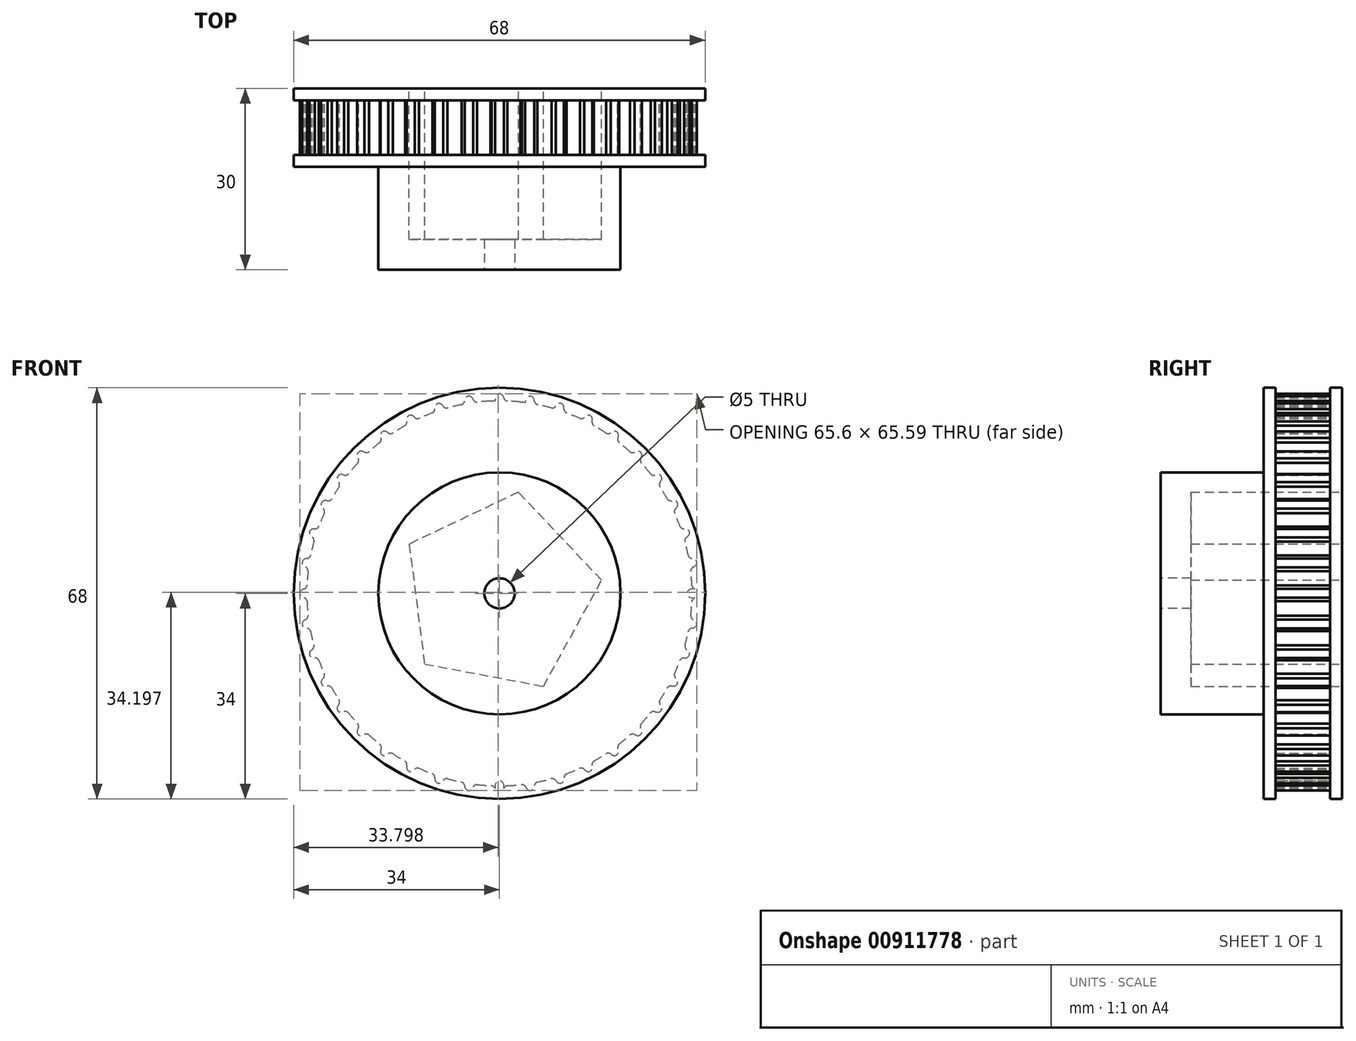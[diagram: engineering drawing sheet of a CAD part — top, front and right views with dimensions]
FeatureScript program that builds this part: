
annotation { "Feature Type Name" : "Feature", "Feature Type Description" : "" }
export const myFeature = defineFeature(function(context is Context, id is Id, definition is map)
    precondition{}
    {
        {
            var Q0;
            Q0=qCreatedBy(makeId("Front.planeOp"),FACE);
            var sketch = newSketch(context, id + "F0", { "sketchPlane" : qUnion([Q0])});
            skCircle(sketch, "E0", {"center": v(0, 0) * mm, "radius": 31.83 * mm});
            skEllipse(sketch, "E1", {"center": v(0, 32) * mm, "majorRadius": 1 * mm, "minorRadius": 0.76 * mm, "majorAxis": v(0, 1)});
            skArc(sketch, "E2", {"start": v(-1.5, 31.8) * mm, "mid": v(-1.02, 31.91) * mm, "end": v(-0.72, 32.3) * mm});
            skArc(sketch, "E3", {"start": v(0.73, 32.28) * mm, "mid": v(1.02, 31.92) * mm, "end": v(1.47, 31.8) * mm});
            skArc(sketch, "E4.1.0", {"start": v(-6.45, 31.17) * mm, "mid": v(-6, 31.36) * mm, "end": v(-5.76, 31.8) * mm});
            skEllipse(sketch, "E4.1.1", {"center": v(-5, 31.6) * mm, "majorRadius": 1 * mm, "minorRadius": 0.76 * mm, "majorAxis": v(-0.16, 0.99)});
            skArc(sketch, "E4.1.2", {"start": v(-4.33, 32) * mm, "mid": v(-3.99, 31.68) * mm, "end": v(-3.52, 31.63) * mm});
            skArc(sketch, "E4.2.0", {"start": v(-11.25, 29.78) * mm, "mid": v(-10.83, 30.04) * mm, "end": v(-10.67, 30.5) * mm});
            skEllipse(sketch, "E4.2.1", {"center": v(-9.89, 30.44) * mm, "majorRadius": 1 * mm, "minorRadius": 0.76 * mm, "majorAxis": v(-0.3, 0.95)});
            skArc(sketch, "E4.2.2", {"start": v(-9.28, 30.93) * mm, "mid": v(-8.9, 30.67) * mm, "end": v(-8.43, 30.7) * mm});
            skArc(sketch, "E4.3.0", {"start": v(-15.77, 27.65) * mm, "mid": v(-15.4, 27.97) * mm, "end": v(-15.3, 28.46) * mm});
            skEllipse(sketch, "E4.3.1", {"center": v(-14.53, 28.52) * mm, "majorRadius": 1 * mm, "minorRadius": 0.76 * mm, "majorAxis": v(-0.45, 0.9)});
            skArc(sketch, "E4.3.2", {"start": v(-14, 29.1) * mm, "mid": v(-13.58, 28.9) * mm, "end": v(-13.12, 29) * mm});
            skArc(sketch, "E4.4.0", {"start": v(-19.9, 24.84) * mm, "mid": v(-19.58, 25.22) * mm, "end": v(-19.57, 25.71) * mm});
            skEllipse(sketch, "E4.4.1", {"center": v(-18.8, 25.9) * mm, "majorRadius": 1 * mm, "minorRadius": 0.76 * mm, "majorAxis": v(-0.59, 0.8)});
            skArc(sketch, "E4.4.2", {"start": v(-18.39, 26.54) * mm, "mid": v(-17.93, 26.42) * mm, "end": v(-17.5, 26.59) * mm});
            skArc(sketch, "E4.5.0", {"start": v(-23.54, 21.42) * mm, "mid": v(-23.29, 21.85) * mm, "end": v(-23.35, 22.33) * mm});
            skEllipse(sketch, "E4.5.1", {"center": v(-22.63, 22.63) * mm, "majorRadius": 1 * mm, "minorRadius": 0.76 * mm, "majorAxis": v(-0.7, 0.7)});
            skArc(sketch, "E4.5.2", {"start": v(-22.31, 23.34) * mm, "mid": v(-21.85, 23.29) * mm, "end": v(-21.44, 23.52) * mm});
            skArc(sketch, "E4.6.0", {"start": v(-26.6, 17.48) * mm, "mid": v(-26.42, 17.93) * mm, "end": v(-26.56, 18.4) * mm});
            skEllipse(sketch, "E4.6.1", {"center": v(-25.9, 18.81) * mm, "majorRadius": 1 * mm, "minorRadius": 0.76 * mm, "majorAxis": v(-0.8, 0.59)});
            skArc(sketch, "E4.6.2", {"start": v(-25.69, 19.56) * mm, "mid": v(-25.22, 19.58) * mm, "end": v(-24.86, 19.88) * mm});
            skArc(sketch, "E4.7.0", {"start": v(-29, 13.1) * mm, "mid": v(-28.9, 13.58) * mm, "end": v(-29.1, 14.03) * mm});
            skEllipse(sketch, "E4.7.1", {"center": v(-28.51, 14.53) * mm, "majorRadius": 1 * mm, "minorRadius": 0.76 * mm, "majorAxis": v(-0.9, 0.45)});
            skArc(sketch, "E4.7.2", {"start": v(-28.43, 15.3) * mm, "mid": v(-27.97, 15.4) * mm, "end": v(-27.66, 15.75) * mm});
            skArc(sketch, "E4.8.0", {"start": v(-30.7, 8.4) * mm, "mid": v(-30.67, 8.9) * mm, "end": v(-30.94, 9.3) * mm});
            skEllipse(sketch, "E4.8.1", {"center": v(-30.44, 9.9) * mm, "majorRadius": 1 * mm, "minorRadius": 0.76 * mm, "majorAxis": v(-0.95, 0.3)});
            skArc(sketch, "E4.8.2", {"start": v(-30.48, 10.67) * mm, "mid": v(-30.04, 10.83) * mm, "end": v(-29.78, 11.22) * mm});
            skArc(sketch, "E4.9.0", {"start": v(-31.64, 3.5) * mm, "mid": v(-31.68, 3.99) * mm, "end": v(-32.02, 4.34) * mm});
            skEllipse(sketch, "E4.9.1", {"center": v(-31.6, 5) * mm, "majorRadius": 1 * mm, "minorRadius": 0.76 * mm, "majorAxis": v(-0.99, 0.16)});
            skArc(sketch, "E4.9.2", {"start": v(-31.77, 5.77) * mm, "mid": v(-31.36, 6) * mm, "end": v(-31.17, 6.43) * mm});
            skArc(sketch, "E4.10.0", {"start": v(-31.8, -1.5) * mm, "mid": v(-31.91, -1.02) * mm, "end": v(-32.3, -0.72) * mm});
            skEllipse(sketch, "E4.10.1", {"center": v(-32, 0) * mm, "majorRadius": 1 * mm, "minorRadius": 0.76 * mm, "majorAxis": v(-1, 0)});
            skArc(sketch, "E4.10.2", {"start": v(-32.28, 0.73) * mm, "mid": v(-31.92, 1.02) * mm, "end": v(-31.8, 1.47) * mm});
            skArc(sketch, "E4.11.0", {"start": v(-31.17, -6.45) * mm, "mid": v(-31.36, -6) * mm, "end": v(-31.8, -5.76) * mm});
            skEllipse(sketch, "E4.11.1", {"center": v(-31.6, -5) * mm, "majorRadius": 1 * mm, "minorRadius": 0.76 * mm, "majorAxis": v(-0.99, -0.16)});
            skArc(sketch, "E4.11.2", {"start": v(-32, -4.33) * mm, "mid": v(-31.68, -3.99) * mm, "end": v(-31.63, -3.52) * mm});
            skArc(sketch, "E4.12.0", {"start": v(-29.78, -11.25) * mm, "mid": v(-30.04, -10.83) * mm, "end": v(-30.5, -10.67) * mm});
            skEllipse(sketch, "E4.12.1", {"center": v(-30.44, -9.89) * mm, "majorRadius": 1 * mm, "minorRadius": 0.76 * mm, "majorAxis": v(-0.95, -0.3)});
            skArc(sketch, "E4.12.2", {"start": v(-30.93, -9.28) * mm, "mid": v(-30.67, -8.9) * mm, "end": v(-30.7, -8.43) * mm});
            skArc(sketch, "E4.13.0", {"start": v(-27.65, -15.77) * mm, "mid": v(-27.97, -15.4) * mm, "end": v(-28.46, -15.3) * mm});
            skEllipse(sketch, "E4.13.1", {"center": v(-28.52, -14.53) * mm, "majorRadius": 1 * mm, "minorRadius": 0.76 * mm, "majorAxis": v(-0.9, -0.45)});
            skArc(sketch, "E4.13.2", {"start": v(-29.1, -14) * mm, "mid": v(-28.9, -13.58) * mm, "end": v(-29, -13.12) * mm});
            skArc(sketch, "E4.14.0", {"start": v(-24.84, -19.9) * mm, "mid": v(-25.22, -19.58) * mm, "end": v(-25.71, -19.57) * mm});
            skEllipse(sketch, "E4.14.1", {"center": v(-25.9, -18.8) * mm, "majorRadius": 1 * mm, "minorRadius": 0.76 * mm, "majorAxis": v(-0.8, -0.59)});
            skArc(sketch, "E4.14.2", {"start": v(-26.54, -18.39) * mm, "mid": v(-26.42, -17.93) * mm, "end": v(-26.59, -17.5) * mm});
            skArc(sketch, "E4.15.0", {"start": v(-21.42, -23.54) * mm, "mid": v(-21.85, -23.29) * mm, "end": v(-22.33, -23.35) * mm});
            skEllipse(sketch, "E4.15.1", {"center": v(-22.63, -22.63) * mm, "majorRadius": 1 * mm, "minorRadius": 0.76 * mm, "majorAxis": v(-0.7, -0.7)});
            skArc(sketch, "E4.15.2", {"start": v(-23.34, -22.31) * mm, "mid": v(-23.29, -21.85) * mm, "end": v(-23.52, -21.44) * mm});
            skArc(sketch, "E4.16.0", {"start": v(-17.48, -26.6) * mm, "mid": v(-17.93, -26.42) * mm, "end": v(-18.4, -26.56) * mm});
            skEllipse(sketch, "E4.16.1", {"center": v(-18.81, -25.9) * mm, "majorRadius": 1 * mm, "minorRadius": 0.76 * mm, "majorAxis": v(-0.59, -0.8)});
            skArc(sketch, "E4.16.2", {"start": v(-19.56, -25.69) * mm, "mid": v(-19.58, -25.22) * mm, "end": v(-19.88, -24.86) * mm});
            skArc(sketch, "E4.17.0", {"start": v(-13.1, -29) * mm, "mid": v(-13.58, -28.9) * mm, "end": v(-14.03, -29.1) * mm});
            skEllipse(sketch, "E4.17.1", {"center": v(-14.53, -28.51) * mm, "majorRadius": 1 * mm, "minorRadius": 0.76 * mm, "majorAxis": v(-0.45, -0.9)});
            skArc(sketch, "E4.17.2", {"start": v(-15.3, -28.43) * mm, "mid": v(-15.4, -27.97) * mm, "end": v(-15.75, -27.66) * mm});
            skArc(sketch, "E4.18.0", {"start": v(-8.4, -30.7) * mm, "mid": v(-8.9, -30.67) * mm, "end": v(-9.3, -30.94) * mm});
            skEllipse(sketch, "E4.18.1", {"center": v(-9.9, -30.44) * mm, "majorRadius": 1 * mm, "minorRadius": 0.76 * mm, "majorAxis": v(-0.3, -0.95)});
            skArc(sketch, "E4.18.2", {"start": v(-10.67, -30.48) * mm, "mid": v(-10.83, -30.04) * mm, "end": v(-11.22, -29.78) * mm});
            skArc(sketch, "E4.19.0", {"start": v(-3.5, -31.64) * mm, "mid": v(-3.99, -31.68) * mm, "end": v(-4.34, -32.02) * mm});
            skEllipse(sketch, "E4.19.1", {"center": v(-5, -31.6) * mm, "majorRadius": 1 * mm, "minorRadius": 0.76 * mm, "majorAxis": v(-0.16, -0.99)});
            skArc(sketch, "E4.19.2", {"start": v(-5.77, -31.77) * mm, "mid": v(-6, -31.36) * mm, "end": v(-6.43, -31.17) * mm});
            skArc(sketch, "E4.20.0", {"start": v(1.5, -31.8) * mm, "mid": v(1.02, -31.91) * mm, "end": v(0.72, -32.3) * mm});
            skEllipse(sketch, "E4.20.1", {"center": v(0, -32) * mm, "majorRadius": 1 * mm, "minorRadius": 0.76 * mm, "majorAxis": v(0, -1)});
            skArc(sketch, "E4.20.2", {"start": v(-0.73, -32.28) * mm, "mid": v(-1.02, -31.92) * mm, "end": v(-1.47, -31.8) * mm});
            skArc(sketch, "E4.21.0", {"start": v(6.45, -31.17) * mm, "mid": v(6, -31.36) * mm, "end": v(5.76, -31.8) * mm});
            skEllipse(sketch, "E4.21.1", {"center": v(5, -31.6) * mm, "majorRadius": 1 * mm, "minorRadius": 0.76 * mm, "majorAxis": v(0.16, -0.99)});
            skArc(sketch, "E4.21.2", {"start": v(4.33, -32) * mm, "mid": v(3.99, -31.68) * mm, "end": v(3.52, -31.63) * mm});
            skArc(sketch, "E4.22.0", {"start": v(11.25, -29.78) * mm, "mid": v(10.83, -30.04) * mm, "end": v(10.67, -30.5) * mm});
            skEllipse(sketch, "E4.22.1", {"center": v(9.89, -30.44) * mm, "majorRadius": 1 * mm, "minorRadius": 0.76 * mm, "majorAxis": v(0.3, -0.95)});
            skArc(sketch, "E4.22.2", {"start": v(9.28, -30.93) * mm, "mid": v(8.9, -30.67) * mm, "end": v(8.43, -30.7) * mm});
            skArc(sketch, "E4.23.0", {"start": v(15.77, -27.65) * mm, "mid": v(15.4, -27.97) * mm, "end": v(15.3, -28.46) * mm});
            skEllipse(sketch, "E4.23.1", {"center": v(14.53, -28.52) * mm, "majorRadius": 1 * mm, "minorRadius": 0.76 * mm, "majorAxis": v(0.45, -0.9)});
            skArc(sketch, "E4.23.2", {"start": v(14, -29.1) * mm, "mid": v(13.58, -28.9) * mm, "end": v(13.12, -29) * mm});
            skArc(sketch, "E4.24.0", {"start": v(19.9, -24.84) * mm, "mid": v(19.58, -25.22) * mm, "end": v(19.57, -25.71) * mm});
            skEllipse(sketch, "E4.24.1", {"center": v(18.8, -25.9) * mm, "majorRadius": 1 * mm, "minorRadius": 0.76 * mm, "majorAxis": v(0.59, -0.8)});
            skArc(sketch, "E4.24.2", {"start": v(18.39, -26.54) * mm, "mid": v(17.93, -26.42) * mm, "end": v(17.5, -26.59) * mm});
            skArc(sketch, "E4.25.0", {"start": v(23.54, -21.42) * mm, "mid": v(23.29, -21.85) * mm, "end": v(23.35, -22.33) * mm});
            skEllipse(sketch, "E4.25.1", {"center": v(22.63, -22.63) * mm, "majorRadius": 1 * mm, "minorRadius": 0.76 * mm, "majorAxis": v(0.7, -0.7)});
            skArc(sketch, "E4.25.2", {"start": v(22.31, -23.34) * mm, "mid": v(21.85, -23.29) * mm, "end": v(21.44, -23.52) * mm});
            skArc(sketch, "E4.26.0", {"start": v(26.6, -17.48) * mm, "mid": v(26.42, -17.93) * mm, "end": v(26.56, -18.4) * mm});
            skEllipse(sketch, "E4.26.1", {"center": v(25.9, -18.81) * mm, "majorRadius": 1 * mm, "minorRadius": 0.76 * mm, "majorAxis": v(0.8, -0.59)});
            skArc(sketch, "E4.26.2", {"start": v(25.69, -19.56) * mm, "mid": v(25.22, -19.58) * mm, "end": v(24.86, -19.88) * mm});
            skArc(sketch, "E4.27.0", {"start": v(29, -13.1) * mm, "mid": v(28.9, -13.58) * mm, "end": v(29.1, -14.03) * mm});
            skEllipse(sketch, "E4.27.1", {"center": v(28.51, -14.53) * mm, "majorRadius": 1 * mm, "minorRadius": 0.76 * mm, "majorAxis": v(0.9, -0.45)});
            skArc(sketch, "E4.27.2", {"start": v(28.43, -15.3) * mm, "mid": v(27.97, -15.4) * mm, "end": v(27.66, -15.75) * mm});
            skArc(sketch, "E4.28.0", {"start": v(30.7, -8.4) * mm, "mid": v(30.67, -8.9) * mm, "end": v(30.94, -9.3) * mm});
            skEllipse(sketch, "E4.28.1", {"center": v(30.44, -9.9) * mm, "majorRadius": 1 * mm, "minorRadius": 0.76 * mm, "majorAxis": v(0.95, -0.3)});
            skArc(sketch, "E4.28.2", {"start": v(30.48, -10.67) * mm, "mid": v(30.04, -10.83) * mm, "end": v(29.78, -11.22) * mm});
            skArc(sketch, "E4.29.0", {"start": v(31.64, -3.5) * mm, "mid": v(31.68, -3.99) * mm, "end": v(32.02, -4.34) * mm});
            skEllipse(sketch, "E4.29.1", {"center": v(31.6, -5) * mm, "majorRadius": 1 * mm, "minorRadius": 0.76 * mm, "majorAxis": v(0.99, -0.16)});
            skArc(sketch, "E4.29.2", {"start": v(31.77, -5.77) * mm, "mid": v(31.36, -6) * mm, "end": v(31.17, -6.43) * mm});
            skArc(sketch, "E4.30.0", {"start": v(31.8, 1.5) * mm, "mid": v(31.91, 1.02) * mm, "end": v(32.3, 0.72) * mm});
            skEllipse(sketch, "E4.30.1", {"center": v(32, 0) * mm, "majorRadius": 1 * mm, "minorRadius": 0.76 * mm, "majorAxis": v(1, 0)});
            skArc(sketch, "E4.30.2", {"start": v(32.28, -0.73) * mm, "mid": v(31.92, -1.02) * mm, "end": v(31.8, -1.47) * mm});
            skArc(sketch, "E4.31.0", {"start": v(31.17, 6.45) * mm, "mid": v(31.36, 6) * mm, "end": v(31.8, 5.76) * mm});
            skEllipse(sketch, "E4.31.1", {"center": v(31.6, 5) * mm, "majorRadius": 1 * mm, "minorRadius": 0.76 * mm, "majorAxis": v(0.99, 0.16)});
            skArc(sketch, "E4.31.2", {"start": v(32, 4.33) * mm, "mid": v(31.68, 3.99) * mm, "end": v(31.63, 3.52) * mm});
            skArc(sketch, "E4.32.0", {"start": v(29.78, 11.25) * mm, "mid": v(30.04, 10.83) * mm, "end": v(30.5, 10.67) * mm});
            skEllipse(sketch, "E4.32.1", {"center": v(30.44, 9.89) * mm, "majorRadius": 1 * mm, "minorRadius": 0.76 * mm, "majorAxis": v(0.95, 0.3)});
            skArc(sketch, "E4.32.2", {"start": v(30.93, 9.28) * mm, "mid": v(30.67, 8.9) * mm, "end": v(30.7, 8.43) * mm});
            skArc(sketch, "E4.33.0", {"start": v(27.65, 15.77) * mm, "mid": v(27.97, 15.4) * mm, "end": v(28.46, 15.3) * mm});
            skEllipse(sketch, "E4.33.1", {"center": v(28.52, 14.53) * mm, "majorRadius": 1 * mm, "minorRadius": 0.76 * mm, "majorAxis": v(0.9, 0.45)});
            skArc(sketch, "E4.33.2", {"start": v(29.1, 14) * mm, "mid": v(28.9, 13.58) * mm, "end": v(29, 13.12) * mm});
            skArc(sketch, "E4.34.0", {"start": v(24.84, 19.9) * mm, "mid": v(25.22, 19.58) * mm, "end": v(25.71, 19.57) * mm});
            skEllipse(sketch, "E4.34.1", {"center": v(25.9, 18.8) * mm, "majorRadius": 1 * mm, "minorRadius": 0.76 * mm, "majorAxis": v(0.8, 0.59)});
            skArc(sketch, "E4.34.2", {"start": v(26.54, 18.39) * mm, "mid": v(26.42, 17.93) * mm, "end": v(26.59, 17.5) * mm});
            skArc(sketch, "E4.35.0", {"start": v(21.42, 23.54) * mm, "mid": v(21.85, 23.29) * mm, "end": v(22.33, 23.35) * mm});
            skEllipse(sketch, "E4.35.1", {"center": v(22.63, 22.63) * mm, "majorRadius": 1 * mm, "minorRadius": 0.76 * mm, "majorAxis": v(0.7, 0.7)});
            skArc(sketch, "E4.35.2", {"start": v(23.34, 22.31) * mm, "mid": v(23.29, 21.85) * mm, "end": v(23.52, 21.44) * mm});
            skArc(sketch, "E4.36.0", {"start": v(17.48, 26.6) * mm, "mid": v(17.93, 26.42) * mm, "end": v(18.4, 26.56) * mm});
            skEllipse(sketch, "E4.36.1", {"center": v(18.81, 25.9) * mm, "majorRadius": 1 * mm, "minorRadius": 0.76 * mm, "majorAxis": v(0.59, 0.8)});
            skArc(sketch, "E4.36.2", {"start": v(19.56, 25.69) * mm, "mid": v(19.58, 25.22) * mm, "end": v(19.88, 24.86) * mm});
            skArc(sketch, "E4.37.0", {"start": v(13.1, 29) * mm, "mid": v(13.58, 28.9) * mm, "end": v(14.03, 29.1) * mm});
            skEllipse(sketch, "E4.37.1", {"center": v(14.53, 28.51) * mm, "majorRadius": 1 * mm, "minorRadius": 0.76 * mm, "majorAxis": v(0.45, 0.9)});
            skArc(sketch, "E4.37.2", {"start": v(15.3, 28.43) * mm, "mid": v(15.4, 27.97) * mm, "end": v(15.75, 27.66) * mm});
            skArc(sketch, "E4.38.0", {"start": v(8.4, 30.7) * mm, "mid": v(8.9, 30.67) * mm, "end": v(9.3, 30.94) * mm});
            skEllipse(sketch, "E4.38.1", {"center": v(9.9, 30.44) * mm, "majorRadius": 1 * mm, "minorRadius": 0.76 * mm, "majorAxis": v(0.3, 0.95)});
            skArc(sketch, "E4.38.2", {"start": v(10.67, 30.48) * mm, "mid": v(10.83, 30.04) * mm, "end": v(11.22, 29.78) * mm});
            skArc(sketch, "E4.39.0", {"start": v(3.5, 31.64) * mm, "mid": v(3.99, 31.68) * mm, "end": v(4.34, 32.02) * mm});
            skEllipse(sketch, "E4.39.1", {"center": v(5, 31.6) * mm, "majorRadius": 1 * mm, "minorRadius": 0.76 * mm, "majorAxis": v(0.16, 0.99)});
            skArc(sketch, "E4.39.2", {"start": v(5.77, 31.77) * mm, "mid": v(6, 31.36) * mm, "end": v(6.43, 31.17) * mm});
            skSolve(sketch);
        }
        {
            var Q0;
            {var subQ0=sQuery(id+"F0.wireOp",EDGE,"E4.9.1");var subQ1=sQuery(id+"F0.wireOp",EDGE,"E0");var subQ2=makeQuery(id+"F0.imprint","INTERSECT",VERTEX,{"disambiguationData":[OD(0.0)],"derivedFrom":[subQ1,subQ0]});Q0=makeQuery(id+"F0.imprint","IMPRINT",FACE,{"disambiguationData":[TD([[makeQuery(id+"F0.imprint","IMPRINT",EDGE,{"disambiguationData":[TD([[subQ2,-1.0]])],"derivedFrom":subQ1}),-1.0]])]});}
            var Q1;
            {var subQ1=sQuery(id+"F0.wireOp",EDGE,"E0");var subQ208=sQuery(id+"F0.wireOp",EDGE,"E4.30.0");var subQ210=makeQuery(id+"F0.imprint","INTERSECT",VERTEX,{"disambiguationData":[OD(1.0)],"derivedFrom":[subQ1,subQ208]});Q1=makeQuery(id+"F0.imprint","IMPRINT",FACE,{"disambiguationData":[TD([[makeQuery(id+"F0.imprint","IMPRINT",EDGE,{"disambiguationData":[TD([[subQ210,1.0]])],"derivedFrom":subQ1}),1.0]])]});}
            var Q2;
            {var subQ0=sQuery(id+"F0.wireOp",EDGE,"E4.4.1");var subQ1=sQuery(id+"F0.wireOp",EDGE,"E0");var subQ2=makeQuery(id+"F0.imprint","INTERSECT",VERTEX,{"disambiguationData":[OD(0.0)],"derivedFrom":[subQ1,subQ0]});Q2=makeQuery(id+"F0.imprint","IMPRINT",FACE,{"disambiguationData":[TD([[makeQuery(id+"F0.imprint","IMPRINT",EDGE,{"disambiguationData":[TD([[subQ2,-1.0]])],"derivedFrom":subQ1}),1.0]])]});}
            var Q3;
            {var subQ0=sQuery(id+"F0.wireOp",EDGE,"E4.8.0");var subQ1=sQuery(id+"F0.wireOp",EDGE,"E0");var subQ2=makeQuery(id+"F0.imprint","INTERSECT",VERTEX,{"disambiguationData":[OD(1.0)],"derivedFrom":[subQ1,subQ0]});Q3=makeQuery(id+"F0.imprint","IMPRINT",FACE,{"disambiguationData":[TD([[makeQuery(id+"F0.imprint","IMPRINT",EDGE,{"disambiguationData":[TD([[subQ2,1.0]])],"derivedFrom":subQ1}),-1.0]])]});}
            var Q4;
            {var subQ0=sQuery(id+"F0.wireOp",EDGE,"E4.32.1");var subQ1=sQuery(id+"F0.wireOp",EDGE,"E0");var subQ2=makeQuery(id+"F0.imprint","INTERSECT",VERTEX,{"disambiguationData":[OD(0.0)],"derivedFrom":[subQ1,subQ0]});Q4=makeQuery(id+"F0.imprint","IMPRINT",FACE,{"disambiguationData":[TD([[makeQuery(id+"F0.imprint","IMPRINT",EDGE,{"disambiguationData":[TD([[subQ2,-1.0]])],"derivedFrom":subQ1}),-1.0]])]});}
            var Q5;
            {var subQ0=sQuery(id+"F0.wireOp",EDGE,"E4.30.1");var subQ1=sQuery(id+"F0.wireOp",EDGE,"E0");var subQ2=makeQuery(id+"F0.imprint","INTERSECT",VERTEX,{"disambiguationData":[OD(0.0)],"derivedFrom":[subQ1,subQ0]});Q5=makeQuery(id+"F0.imprint","IMPRINT",FACE,{"disambiguationData":[TD([[makeQuery(id+"F0.imprint","IMPRINT",EDGE,{"disambiguationData":[TD([[subQ2,1.0]])],"derivedFrom":subQ1}),1.0]])]});}
            var Q6;
            {var subQ0=sQuery(id+"F0.wireOp",EDGE,"E4.36.1");var subQ1=sQuery(id+"F0.wireOp",EDGE,"E0");var subQ2=makeQuery(id+"F0.imprint","INTERSECT",VERTEX,{"disambiguationData":[OD(0.0)],"derivedFrom":[subQ1,subQ0]});Q6=makeQuery(id+"F0.imprint","IMPRINT",FACE,{"disambiguationData":[TD([[makeQuery(id+"F0.imprint","IMPRINT",EDGE,{"disambiguationData":[TD([[subQ2,-1.0]])],"derivedFrom":subQ1}),1.0]])]});}
            var Q7;
            {var subQ0=sQuery(id+"F0.wireOp",EDGE,"E4.10.1");var subQ1=sQuery(id+"F0.wireOp",EDGE,"E0");var subQ2=makeQuery(id+"F0.imprint","INTERSECT",VERTEX,{"disambiguationData":[OD(0.0)],"derivedFrom":[subQ1,subQ0]});Q7=makeQuery(id+"F0.imprint","IMPRINT",FACE,{"disambiguationData":[TD([[makeQuery(id+"F0.imprint","IMPRINT",EDGE,{"disambiguationData":[TD([[subQ2,-1.0]])],"derivedFrom":subQ1}),1.0]])]});}
            var Q8;
            {var subQ0=sQuery(id+"F0.wireOp",EDGE,"E4.6.1");var subQ1=sQuery(id+"F0.wireOp",EDGE,"E0");var subQ2=makeQuery(id+"F0.imprint","INTERSECT",VERTEX,{"disambiguationData":[OD(0.0)],"derivedFrom":[subQ1,subQ0]});Q8=makeQuery(id+"F0.imprint","IMPRINT",FACE,{"disambiguationData":[TD([[makeQuery(id+"F0.imprint","IMPRINT",EDGE,{"disambiguationData":[TD([[subQ2,-1.0]])],"derivedFrom":subQ1}),1.0]])]});}
            var Q9;
            {var subQ0=sQuery(id+"F0.wireOp",EDGE,"E4.26.1");var subQ1=sQuery(id+"F0.wireOp",EDGE,"E0");var subQ2=makeQuery(id+"F0.imprint","INTERSECT",VERTEX,{"disambiguationData":[OD(0.0)],"derivedFrom":[subQ1,subQ0]});Q9=makeQuery(id+"F0.imprint","IMPRINT",FACE,{"disambiguationData":[TD([[makeQuery(id+"F0.imprint","IMPRINT",EDGE,{"disambiguationData":[TD([[subQ2,-1.0]])],"derivedFrom":subQ1}),1.0]])]});}
            var Q10;
            {var subQ0=sQuery(id+"F0.wireOp",EDGE,"E4.21.1");var subQ1=sQuery(id+"F0.wireOp",EDGE,"E0");var subQ2=makeQuery(id+"F0.imprint","INTERSECT",VERTEX,{"disambiguationData":[OD(0.0)],"derivedFrom":[subQ1,subQ0]});Q10=makeQuery(id+"F0.imprint","IMPRINT",FACE,{"disambiguationData":[TD([[makeQuery(id+"F0.imprint","IMPRINT",EDGE,{"disambiguationData":[TD([[subQ2,-1.0]])],"derivedFrom":subQ1}),1.0]])]});}
            var Q11;
            {var subQ0=sQuery(id+"F0.wireOp",EDGE,"E4.18.1");var subQ1=sQuery(id+"F0.wireOp",EDGE,"E0");var subQ2=makeQuery(id+"F0.imprint","INTERSECT",VERTEX,{"disambiguationData":[OD(0.0)],"derivedFrom":[subQ1,subQ0]});Q11=makeQuery(id+"F0.imprint","IMPRINT",FACE,{"disambiguationData":[TD([[makeQuery(id+"F0.imprint","IMPRINT",EDGE,{"disambiguationData":[TD([[subQ2,-1.0]])],"derivedFrom":subQ1}),-1.0]])]});}
            var Q12;
            {var subQ0=sQuery(id+"F0.wireOp",EDGE,"E1");var subQ1=sQuery(id+"F0.wireOp",EDGE,"E0");var subQ2=makeQuery(id+"F0.imprint","INTERSECT",VERTEX,{"disambiguationData":[OD(0.0)],"derivedFrom":[subQ1,subQ0]});Q12=makeQuery(id+"F0.imprint","IMPRINT",FACE,{"disambiguationData":[TD([[makeQuery(id+"F0.imprint","IMPRINT",EDGE,{"disambiguationData":[TD([[subQ2,-1.0]])],"derivedFrom":subQ1}),1.0]])]});}
            var Q13;
            {var subQ0=sQuery(id+"F0.wireOp",EDGE,"E4.33.1");var subQ1=sQuery(id+"F0.wireOp",EDGE,"E0");var subQ2=makeQuery(id+"F0.imprint","INTERSECT",VERTEX,{"disambiguationData":[OD(0.0)],"derivedFrom":[subQ1,subQ0]});Q13=makeQuery(id+"F0.imprint","IMPRINT",FACE,{"disambiguationData":[TD([[makeQuery(id+"F0.imprint","IMPRINT",EDGE,{"disambiguationData":[TD([[subQ2,-1.0]])],"derivedFrom":subQ1}),1.0]])]});}
            var Q14;
            {var subQ0=sQuery(id+"F0.wireOp",EDGE,"E4.34.1");var subQ1=sQuery(id+"F0.wireOp",EDGE,"E0");var subQ2=makeQuery(id+"F0.imprint","INTERSECT",VERTEX,{"disambiguationData":[OD(0.0)],"derivedFrom":[subQ1,subQ0]});Q14=makeQuery(id+"F0.imprint","IMPRINT",FACE,{"disambiguationData":[TD([[makeQuery(id+"F0.imprint","IMPRINT",EDGE,{"disambiguationData":[TD([[subQ2,-1.0]])],"derivedFrom":subQ1}),1.0]])]});}
            var Q15;
            {var subQ0=sQuery(id+"F0.wireOp",EDGE,"E4.17.0");var subQ1=sQuery(id+"F0.wireOp",EDGE,"E0");var subQ2=makeQuery(id+"F0.imprint","INTERSECT",VERTEX,{"disambiguationData":[OD(1.0)],"derivedFrom":[subQ1,subQ0]});Q15=makeQuery(id+"F0.imprint","IMPRINT",FACE,{"disambiguationData":[TD([[makeQuery(id+"F0.imprint","IMPRINT",EDGE,{"disambiguationData":[TD([[subQ2,1.0]])],"derivedFrom":subQ1}),-1.0]])]});}
            var Q16;
            {var subQ0=sQuery(id+"F0.wireOp",EDGE,"E4.39.1");var subQ1=sQuery(id+"F0.wireOp",EDGE,"E0");var subQ2=makeQuery(id+"F0.imprint","INTERSECT",VERTEX,{"disambiguationData":[OD(0.0)],"derivedFrom":[subQ1,subQ0]});Q16=makeQuery(id+"F0.imprint","IMPRINT",FACE,{"disambiguationData":[TD([[makeQuery(id+"F0.imprint","IMPRINT",EDGE,{"disambiguationData":[TD([[subQ2,-1.0]])],"derivedFrom":subQ1}),1.0]])]});}
            var Q17;
            {var subQ0=sQuery(id+"F0.wireOp",EDGE,"E4.7.1");var subQ1=sQuery(id+"F0.wireOp",EDGE,"E0");var subQ2=makeQuery(id+"F0.imprint","INTERSECT",VERTEX,{"disambiguationData":[OD(0.0)],"derivedFrom":[subQ1,subQ0]});Q17=makeQuery(id+"F0.imprint","IMPRINT",FACE,{"disambiguationData":[TD([[makeQuery(id+"F0.imprint","IMPRINT",EDGE,{"disambiguationData":[TD([[subQ2,-1.0]])],"derivedFrom":subQ1}),-1.0]])]});}
            var Q18;
            {var subQ0=sQuery(id+"F0.wireOp",EDGE,"E4.33.1");var subQ1=sQuery(id+"F0.wireOp",EDGE,"E0");var subQ2=makeQuery(id+"F0.imprint","INTERSECT",VERTEX,{"disambiguationData":[OD(0.0)],"derivedFrom":[subQ1,subQ0]});Q18=makeQuery(id+"F0.imprint","IMPRINT",FACE,{"disambiguationData":[TD([[makeQuery(id+"F0.imprint","IMPRINT",EDGE,{"disambiguationData":[TD([[subQ2,-1.0]])],"derivedFrom":subQ1}),-1.0]])]});}
            var Q19;
            {var subQ0=sQuery(id+"F0.wireOp",EDGE,"E4.19.1");var subQ1=sQuery(id+"F0.wireOp",EDGE,"E0");var subQ2=makeQuery(id+"F0.imprint","INTERSECT",VERTEX,{"disambiguationData":[OD(0.0)],"derivedFrom":[subQ1,subQ0]});Q19=makeQuery(id+"F0.imprint","IMPRINT",FACE,{"disambiguationData":[TD([[makeQuery(id+"F0.imprint","IMPRINT",EDGE,{"disambiguationData":[TD([[subQ2,-1.0]])],"derivedFrom":subQ1}),-1.0]])]});}
            var Q20;
            {var subQ0=sQuery(id+"F0.wireOp",EDGE,"E4.19.1");var subQ1=sQuery(id+"F0.wireOp",EDGE,"E0");var subQ2=makeQuery(id+"F0.imprint","INTERSECT",VERTEX,{"disambiguationData":[OD(0.0)],"derivedFrom":[subQ1,subQ0]});Q20=makeQuery(id+"F0.imprint","IMPRINT",FACE,{"disambiguationData":[TD([[makeQuery(id+"F0.imprint","IMPRINT",EDGE,{"disambiguationData":[TD([[subQ2,-1.0]])],"derivedFrom":subQ1}),1.0]])]});}
            var Q21;
            {var subQ0=sQuery(id+"F0.wireOp",EDGE,"E4.6.2");var subQ1=sQuery(id+"F0.wireOp",EDGE,"E0");var subQ2=makeQuery(id+"F0.imprint","INTERSECT",VERTEX,{"derivedFrom":[subQ1,subQ0]});Q21=makeQuery(id+"F0.imprint","IMPRINT",FACE,{"disambiguationData":[TD([[makeQuery(id+"F0.imprint","IMPRINT",EDGE,{"disambiguationData":[TD([[subQ2,-1.0]])],"derivedFrom":subQ1}),-1.0]])]});}
            var Q22;
            {var subQ0=sQuery(id+"F0.wireOp",EDGE,"E4.36.1");var subQ1=sQuery(id+"F0.wireOp",EDGE,"E0");var subQ2=makeQuery(id+"F0.imprint","INTERSECT",VERTEX,{"disambiguationData":[OD(0.0)],"derivedFrom":[subQ1,subQ0]});Q22=makeQuery(id+"F0.imprint","IMPRINT",FACE,{"disambiguationData":[TD([[makeQuery(id+"F0.imprint","IMPRINT",EDGE,{"disambiguationData":[TD([[subQ2,-1.0]])],"derivedFrom":subQ1}),-1.0]])]});}
            var Q23;
            {var subQ0=sQuery(id+"F0.wireOp",EDGE,"E4.37.1");var subQ1=sQuery(id+"F0.wireOp",EDGE,"E0");var subQ2=makeQuery(id+"F0.imprint","INTERSECT",VERTEX,{"disambiguationData":[OD(0.0)],"derivedFrom":[subQ1,subQ0]});Q23=makeQuery(id+"F0.imprint","IMPRINT",FACE,{"disambiguationData":[TD([[makeQuery(id+"F0.imprint","IMPRINT",EDGE,{"disambiguationData":[TD([[subQ2,-1.0]])],"derivedFrom":subQ1}),-1.0]])]});}
            var Q24;
            {var subQ0=sQuery(id+"F0.wireOp",EDGE,"E4.27.1");var subQ1=sQuery(id+"F0.wireOp",EDGE,"E0");var subQ2=makeQuery(id+"F0.imprint","INTERSECT",VERTEX,{"disambiguationData":[OD(0.0)],"derivedFrom":[subQ1,subQ0]});Q24=makeQuery(id+"F0.imprint","IMPRINT",FACE,{"disambiguationData":[TD([[makeQuery(id+"F0.imprint","IMPRINT",EDGE,{"disambiguationData":[TD([[subQ2,-1.0]])],"derivedFrom":subQ1}),1.0]])]});}
            var Q25;
            {var subQ0=sQuery(id+"F0.wireOp",EDGE,"E4.26.1");var subQ1=sQuery(id+"F0.wireOp",EDGE,"E0");var subQ2=makeQuery(id+"F0.imprint","INTERSECT",VERTEX,{"disambiguationData":[OD(0.0)],"derivedFrom":[subQ1,subQ0]});Q25=makeQuery(id+"F0.imprint","IMPRINT",FACE,{"disambiguationData":[TD([[makeQuery(id+"F0.imprint","IMPRINT",EDGE,{"disambiguationData":[TD([[subQ2,-1.0]])],"derivedFrom":subQ1}),-1.0]])]});}
            var Q26;
            {var subQ0=sQuery(id+"F0.wireOp",EDGE,"E4.10.1");var subQ1=sQuery(id+"F0.wireOp",EDGE,"E0");var subQ2=makeQuery(id+"F0.imprint","INTERSECT",VERTEX,{"disambiguationData":[OD(0.0)],"derivedFrom":[subQ1,subQ0]});Q26=makeQuery(id+"F0.imprint","IMPRINT",FACE,{"disambiguationData":[TD([[makeQuery(id+"F0.imprint","IMPRINT",EDGE,{"disambiguationData":[TD([[subQ2,-1.0]])],"derivedFrom":subQ1}),-1.0]])]});}
            var Q27;
            {var subQ0=sQuery(id+"F0.wireOp",EDGE,"E4.15.1");var subQ1=sQuery(id+"F0.wireOp",EDGE,"E0");var subQ2=makeQuery(id+"F0.imprint","INTERSECT",VERTEX,{"disambiguationData":[OD(0.0)],"derivedFrom":[subQ1,subQ0]});Q27=makeQuery(id+"F0.imprint","IMPRINT",FACE,{"disambiguationData":[TD([[makeQuery(id+"F0.imprint","IMPRINT",EDGE,{"disambiguationData":[TD([[subQ2,-1.0]])],"derivedFrom":subQ1}),-1.0]])]});}
            var Q28;
            {var subQ0=sQuery(id+"F0.wireOp",EDGE,"E4.20.1");var subQ1=sQuery(id+"F0.wireOp",EDGE,"E0");var subQ2=makeQuery(id+"F0.imprint","INTERSECT",VERTEX,{"disambiguationData":[OD(0.0)],"derivedFrom":[subQ1,subQ0]});Q28=makeQuery(id+"F0.imprint","IMPRINT",FACE,{"disambiguationData":[TD([[makeQuery(id+"F0.imprint","IMPRINT",EDGE,{"disambiguationData":[TD([[subQ2,-1.0]])],"derivedFrom":subQ1}),1.0]])]});}
            var Q29;
            {var subQ0=sQuery(id+"F0.wireOp",EDGE,"E4.31.1");var subQ1=sQuery(id+"F0.wireOp",EDGE,"E0");var subQ2=makeQuery(id+"F0.imprint","INTERSECT",VERTEX,{"disambiguationData":[OD(0.0)],"derivedFrom":[subQ1,subQ0]});Q29=makeQuery(id+"F0.imprint","IMPRINT",FACE,{"disambiguationData":[TD([[makeQuery(id+"F0.imprint","IMPRINT",EDGE,{"disambiguationData":[TD([[subQ2,-1.0]])],"derivedFrom":subQ1}),-1.0]])]});}
            var Q30;
            {var subQ0=sQuery(id+"F0.wireOp",EDGE,"E4.21.1");var subQ1=sQuery(id+"F0.wireOp",EDGE,"E0");var subQ2=makeQuery(id+"F0.imprint","INTERSECT",VERTEX,{"disambiguationData":[OD(0.0)],"derivedFrom":[subQ1,subQ0]});Q30=makeQuery(id+"F0.imprint","IMPRINT",FACE,{"disambiguationData":[TD([[makeQuery(id+"F0.imprint","IMPRINT",EDGE,{"disambiguationData":[TD([[subQ2,-1.0]])],"derivedFrom":subQ1}),-1.0]])]});}
            var Q31;
            {var subQ0=sQuery(id+"F0.wireOp",EDGE,"E4.18.1");var subQ1=sQuery(id+"F0.wireOp",EDGE,"E0");var subQ2=makeQuery(id+"F0.imprint","INTERSECT",VERTEX,{"disambiguationData":[OD(0.0)],"derivedFrom":[subQ1,subQ0]});Q31=makeQuery(id+"F0.imprint","IMPRINT",FACE,{"disambiguationData":[TD([[makeQuery(id+"F0.imprint","IMPRINT",EDGE,{"disambiguationData":[TD([[subQ2,-1.0]])],"derivedFrom":subQ1}),1.0]])]});}
            var Q32;
            {var subQ0=sQuery(id+"F0.wireOp",EDGE,"E4.37.1");var subQ1=sQuery(id+"F0.wireOp",EDGE,"E0");var subQ2=makeQuery(id+"F0.imprint","INTERSECT",VERTEX,{"disambiguationData":[OD(0.0)],"derivedFrom":[subQ1,subQ0]});Q32=makeQuery(id+"F0.imprint","IMPRINT",FACE,{"disambiguationData":[TD([[makeQuery(id+"F0.imprint","IMPRINT",EDGE,{"disambiguationData":[TD([[subQ2,-1.0]])],"derivedFrom":subQ1}),1.0]])]});}
            var Q33;
            {var subQ0=sQuery(id+"F0.wireOp",EDGE,"E4.1.1");var subQ1=sQuery(id+"F0.wireOp",EDGE,"E0");var subQ2=makeQuery(id+"F0.imprint","INTERSECT",VERTEX,{"disambiguationData":[OD(0.0)],"derivedFrom":[subQ1,subQ0]});Q33=makeQuery(id+"F0.imprint","IMPRINT",FACE,{"disambiguationData":[TD([[makeQuery(id+"F0.imprint","IMPRINT",EDGE,{"disambiguationData":[TD([[subQ2,-1.0]])],"derivedFrom":subQ1}),-1.0]])]});}
            var Q34;
            {var subQ0=sQuery(id+"F0.wireOp",EDGE,"E4.12.1");var subQ1=sQuery(id+"F0.wireOp",EDGE,"E0");var subQ2=makeQuery(id+"F0.imprint","INTERSECT",VERTEX,{"disambiguationData":[OD(0.0)],"derivedFrom":[subQ1,subQ0]});Q34=makeQuery(id+"F0.imprint","IMPRINT",FACE,{"disambiguationData":[TD([[makeQuery(id+"F0.imprint","IMPRINT",EDGE,{"disambiguationData":[TD([[subQ2,-1.0]])],"derivedFrom":subQ1}),-1.0]])]});}
            var Q35;
            {var subQ0=sQuery(id+"F0.wireOp",EDGE,"E4.16.1");var subQ1=sQuery(id+"F0.wireOp",EDGE,"E0");var subQ2=makeQuery(id+"F0.imprint","INTERSECT",VERTEX,{"disambiguationData":[OD(0.0)],"derivedFrom":[subQ1,subQ0]});Q35=makeQuery(id+"F0.imprint","IMPRINT",FACE,{"disambiguationData":[TD([[makeQuery(id+"F0.imprint","IMPRINT",EDGE,{"disambiguationData":[TD([[subQ2,-1.0]])],"derivedFrom":subQ1}),1.0]])]});}
            var Q36;
            {var subQ0=sQuery(id+"F0.wireOp",EDGE,"E4.14.1");var subQ1=sQuery(id+"F0.wireOp",EDGE,"E0");var subQ2=makeQuery(id+"F0.imprint","INTERSECT",VERTEX,{"disambiguationData":[OD(0.0)],"derivedFrom":[subQ1,subQ0]});Q36=makeQuery(id+"F0.imprint","IMPRINT",FACE,{"disambiguationData":[TD([[makeQuery(id+"F0.imprint","IMPRINT",EDGE,{"disambiguationData":[TD([[subQ2,-1.0]])],"derivedFrom":subQ1}),1.0]])]});}
            var Q37;
            {var subQ0=sQuery(id+"F0.wireOp",EDGE,"E4.13.1");var subQ1=sQuery(id+"F0.wireOp",EDGE,"E0");var subQ2=makeQuery(id+"F0.imprint","INTERSECT",VERTEX,{"disambiguationData":[OD(0.0)],"derivedFrom":[subQ1,subQ0]});Q37=makeQuery(id+"F0.imprint","IMPRINT",FACE,{"disambiguationData":[TD([[makeQuery(id+"F0.imprint","IMPRINT",EDGE,{"disambiguationData":[TD([[subQ2,-1.0]])],"derivedFrom":subQ1}),-1.0]])]});}
            var Q38;
            {var subQ0=sQuery(id+"F0.wireOp",EDGE,"E4.25.1");var subQ1=sQuery(id+"F0.wireOp",EDGE,"E0");var subQ2=makeQuery(id+"F0.imprint","INTERSECT",VERTEX,{"disambiguationData":[OD(0.0)],"derivedFrom":[subQ1,subQ0]});Q38=makeQuery(id+"F0.imprint","IMPRINT",FACE,{"disambiguationData":[TD([[makeQuery(id+"F0.imprint","IMPRINT",EDGE,{"disambiguationData":[TD([[subQ2,-1.0]])],"derivedFrom":subQ1}),-1.0]])]});}
            var Q39;
            {var subQ0=sQuery(id+"F0.wireOp",EDGE,"E4.32.1");var subQ1=sQuery(id+"F0.wireOp",EDGE,"E0");var subQ2=makeQuery(id+"F0.imprint","INTERSECT",VERTEX,{"disambiguationData":[OD(0.0)],"derivedFrom":[subQ1,subQ0]});Q39=makeQuery(id+"F0.imprint","IMPRINT",FACE,{"disambiguationData":[TD([[makeQuery(id+"F0.imprint","IMPRINT",EDGE,{"disambiguationData":[TD([[subQ2,-1.0]])],"derivedFrom":subQ1}),1.0]])]});}
            var Q40;
            {var subQ0=sQuery(id+"F0.wireOp",EDGE,"E4.24.1");var subQ1=sQuery(id+"F0.wireOp",EDGE,"E0");var subQ2=makeQuery(id+"F0.imprint","INTERSECT",VERTEX,{"disambiguationData":[OD(0.0)],"derivedFrom":[subQ1,subQ0]});Q40=makeQuery(id+"F0.imprint","IMPRINT",FACE,{"disambiguationData":[TD([[makeQuery(id+"F0.imprint","IMPRINT",EDGE,{"disambiguationData":[TD([[subQ2,-1.0]])],"derivedFrom":subQ1}),-1.0]])]});}
            var Q41;
            {var subQ0=sQuery(id+"F0.wireOp",EDGE,"E4.6.1");var subQ1=sQuery(id+"F0.wireOp",EDGE,"E0");var subQ2=makeQuery(id+"F0.imprint","INTERSECT",VERTEX,{"disambiguationData":[OD(0.0)],"derivedFrom":[subQ1,subQ0]});Q41=makeQuery(id+"F0.imprint","IMPRINT",FACE,{"disambiguationData":[TD([[makeQuery(id+"F0.imprint","IMPRINT",EDGE,{"disambiguationData":[TD([[subQ2,-1.0]])],"derivedFrom":subQ1}),-1.0]])]});}
            var Q42;
            {var subQ0=sQuery(id+"F0.wireOp",EDGE,"E4.11.1");var subQ1=sQuery(id+"F0.wireOp",EDGE,"E0");var subQ2=makeQuery(id+"F0.imprint","INTERSECT",VERTEX,{"disambiguationData":[OD(0.0)],"derivedFrom":[subQ1,subQ0]});Q42=makeQuery(id+"F0.imprint","IMPRINT",FACE,{"disambiguationData":[TD([[makeQuery(id+"F0.imprint","IMPRINT",EDGE,{"disambiguationData":[TD([[subQ2,-1.0]])],"derivedFrom":subQ1}),-1.0]])]});}
            var Q43;
            {var subQ0=sQuery(id+"F0.wireOp",EDGE,"E4.2.1");var subQ1=sQuery(id+"F0.wireOp",EDGE,"E0");var subQ2=makeQuery(id+"F0.imprint","INTERSECT",VERTEX,{"disambiguationData":[OD(0.0)],"derivedFrom":[subQ1,subQ0]});Q43=makeQuery(id+"F0.imprint","IMPRINT",FACE,{"disambiguationData":[TD([[makeQuery(id+"F0.imprint","IMPRINT",EDGE,{"disambiguationData":[TD([[subQ2,-1.0]])],"derivedFrom":subQ1}),-1.0]])]});}
            var Q44;
            {var subQ0=sQuery(id+"F0.wireOp",EDGE,"E4.23.1");var subQ1=sQuery(id+"F0.wireOp",EDGE,"E0");var subQ2=makeQuery(id+"F0.imprint","INTERSECT",VERTEX,{"disambiguationData":[OD(0.0)],"derivedFrom":[subQ1,subQ0]});Q44=makeQuery(id+"F0.imprint","IMPRINT",FACE,{"disambiguationData":[TD([[makeQuery(id+"F0.imprint","IMPRINT",EDGE,{"disambiguationData":[TD([[subQ2,-1.0]])],"derivedFrom":subQ1}),-1.0]])]});}
            var Q45;
            {var subQ0=sQuery(id+"F0.wireOp",EDGE,"E4.3.1");var subQ1=sQuery(id+"F0.wireOp",EDGE,"E0");var subQ2=makeQuery(id+"F0.imprint","INTERSECT",VERTEX,{"disambiguationData":[OD(0.0)],"derivedFrom":[subQ1,subQ0]});Q45=makeQuery(id+"F0.imprint","IMPRINT",FACE,{"disambiguationData":[TD([[makeQuery(id+"F0.imprint","IMPRINT",EDGE,{"disambiguationData":[TD([[subQ2,-1.0]])],"derivedFrom":subQ1}),1.0]])]});}
            var Q46;
            {var subQ0=sQuery(id+"F0.wireOp",EDGE,"E4.16.0");var subQ1=sQuery(id+"F0.wireOp",EDGE,"E0");var subQ2=makeQuery(id+"F0.imprint","INTERSECT",VERTEX,{"disambiguationData":[OD(1.0)],"derivedFrom":[subQ1,subQ0]});Q46=makeQuery(id+"F0.imprint","IMPRINT",FACE,{"disambiguationData":[TD([[makeQuery(id+"F0.imprint","IMPRINT",EDGE,{"disambiguationData":[TD([[subQ2,1.0]])],"derivedFrom":subQ1}),-1.0]])]});}
            var Q47;
            {var subQ0=sQuery(id+"F0.wireOp",EDGE,"E4.14.1");var subQ1=sQuery(id+"F0.wireOp",EDGE,"E0");var subQ2=makeQuery(id+"F0.imprint","INTERSECT",VERTEX,{"disambiguationData":[OD(0.0)],"derivedFrom":[subQ1,subQ0]});Q47=makeQuery(id+"F0.imprint","IMPRINT",FACE,{"disambiguationData":[TD([[makeQuery(id+"F0.imprint","IMPRINT",EDGE,{"disambiguationData":[TD([[subQ2,-1.0]])],"derivedFrom":subQ1}),-1.0]])]});}
            var Q48;
            {var subQ0=sQuery(id+"F0.wireOp",EDGE,"E4.5.1");var subQ1=sQuery(id+"F0.wireOp",EDGE,"E0");var subQ2=makeQuery(id+"F0.imprint","INTERSECT",VERTEX,{"disambiguationData":[OD(0.0)],"derivedFrom":[subQ1,subQ0]});Q48=makeQuery(id+"F0.imprint","IMPRINT",FACE,{"disambiguationData":[TD([[makeQuery(id+"F0.imprint","IMPRINT",EDGE,{"disambiguationData":[TD([[subQ2,-1.0]])],"derivedFrom":subQ1}),-1.0]])]});}
            var Q49;
            {var subQ0=sQuery(id+"F0.wireOp",EDGE,"E4.7.1");var subQ1=sQuery(id+"F0.wireOp",EDGE,"E0");var subQ2=makeQuery(id+"F0.imprint","INTERSECT",VERTEX,{"disambiguationData":[OD(0.0)],"derivedFrom":[subQ1,subQ0]});Q49=makeQuery(id+"F0.imprint","IMPRINT",FACE,{"disambiguationData":[TD([[makeQuery(id+"F0.imprint","IMPRINT",EDGE,{"disambiguationData":[TD([[subQ2,-1.0]])],"derivedFrom":subQ1}),1.0]])]});}
            var Q50;
            {var subQ0=sQuery(id+"F0.wireOp",EDGE,"E4.2.1");var subQ1=sQuery(id+"F0.wireOp",EDGE,"E0");var subQ2=makeQuery(id+"F0.imprint","INTERSECT",VERTEX,{"disambiguationData":[OD(0.0)],"derivedFrom":[subQ1,subQ0]});Q50=makeQuery(id+"F0.imprint","IMPRINT",FACE,{"disambiguationData":[TD([[makeQuery(id+"F0.imprint","IMPRINT",EDGE,{"disambiguationData":[TD([[subQ2,-1.0]])],"derivedFrom":subQ1}),1.0]])]});}
            var Q51;
            {var subQ0=sQuery(id+"F0.wireOp",EDGE,"E4.3.1");var subQ1=sQuery(id+"F0.wireOp",EDGE,"E0");var subQ2=makeQuery(id+"F0.imprint","INTERSECT",VERTEX,{"disambiguationData":[OD(0.0)],"derivedFrom":[subQ1,subQ0]});Q51=makeQuery(id+"F0.imprint","IMPRINT",FACE,{"disambiguationData":[TD([[makeQuery(id+"F0.imprint","IMPRINT",EDGE,{"disambiguationData":[TD([[subQ2,-1.0]])],"derivedFrom":subQ1}),-1.0]])]});}
            var Q52;
            {var subQ0=sQuery(id+"F0.wireOp",EDGE,"E4.11.1");var subQ1=sQuery(id+"F0.wireOp",EDGE,"E0");var subQ2=makeQuery(id+"F0.imprint","INTERSECT",VERTEX,{"disambiguationData":[OD(0.0)],"derivedFrom":[subQ1,subQ0]});Q52=makeQuery(id+"F0.imprint","IMPRINT",FACE,{"disambiguationData":[TD([[makeQuery(id+"F0.imprint","IMPRINT",EDGE,{"disambiguationData":[TD([[subQ2,-1.0]])],"derivedFrom":subQ1}),1.0]])]});}
            var Q53;
            {var subQ0=sQuery(id+"F0.wireOp",EDGE,"E4.17.1");var subQ1=sQuery(id+"F0.wireOp",EDGE,"E0");var subQ2=makeQuery(id+"F0.imprint","INTERSECT",VERTEX,{"disambiguationData":[OD(0.0)],"derivedFrom":[subQ1,subQ0]});Q53=makeQuery(id+"F0.imprint","IMPRINT",FACE,{"disambiguationData":[TD([[makeQuery(id+"F0.imprint","IMPRINT",EDGE,{"disambiguationData":[TD([[subQ2,-1.0]])],"derivedFrom":subQ1}),1.0]])]});}
            var Q54;
            {var subQ0=sQuery(id+"F0.wireOp",EDGE,"E4.15.0");var subQ1=sQuery(id+"F0.wireOp",EDGE,"E0");var subQ2=makeQuery(id+"F0.imprint","INTERSECT",VERTEX,{"disambiguationData":[OD(1.0)],"derivedFrom":[subQ1,subQ0]});Q54=makeQuery(id+"F0.imprint","IMPRINT",FACE,{"disambiguationData":[TD([[makeQuery(id+"F0.imprint","IMPRINT",EDGE,{"disambiguationData":[TD([[subQ2,1.0]])],"derivedFrom":subQ1}),-1.0]])]});}
            var Q55;
            {var subQ0=sQuery(id+"F0.wireOp",EDGE,"E4.25.2");var subQ1=sQuery(id+"F0.wireOp",EDGE,"E0");var subQ2=makeQuery(id+"F0.imprint","INTERSECT",VERTEX,{"derivedFrom":[subQ1,subQ0]});Q55=makeQuery(id+"F0.imprint","IMPRINT",FACE,{"disambiguationData":[TD([[makeQuery(id+"F0.imprint","IMPRINT",EDGE,{"disambiguationData":[TD([[subQ2,-1.0]])],"derivedFrom":subQ1}),-1.0]])]});}
            var Q56;
            {var subQ0=sQuery(id+"F0.wireOp",EDGE,"E4.29.1");var subQ1=sQuery(id+"F0.wireOp",EDGE,"E0");var subQ2=makeQuery(id+"F0.imprint","INTERSECT",VERTEX,{"disambiguationData":[OD(0.0)],"derivedFrom":[subQ1,subQ0]});Q56=makeQuery(id+"F0.imprint","IMPRINT",FACE,{"disambiguationData":[TD([[makeQuery(id+"F0.imprint","IMPRINT",EDGE,{"disambiguationData":[TD([[subQ2,-1.0]])],"derivedFrom":subQ1}),1.0]])]});}
            var Q57;
            {var subQ0=sQuery(id+"F0.wireOp",EDGE,"E4.29.1");var subQ1=sQuery(id+"F0.wireOp",EDGE,"E0");var subQ2=makeQuery(id+"F0.imprint","INTERSECT",VERTEX,{"disambiguationData":[OD(0.0)],"derivedFrom":[subQ1,subQ0]});Q57=makeQuery(id+"F0.imprint","IMPRINT",FACE,{"disambiguationData":[TD([[makeQuery(id+"F0.imprint","IMPRINT",EDGE,{"disambiguationData":[TD([[subQ2,-1.0]])],"derivedFrom":subQ1}),-1.0]])]});}
            var Q58;
            {var subQ0=sQuery(id+"F0.wireOp",EDGE,"E4.28.1");var subQ1=sQuery(id+"F0.wireOp",EDGE,"E0");var subQ2=makeQuery(id+"F0.imprint","INTERSECT",VERTEX,{"disambiguationData":[OD(0.0)],"derivedFrom":[subQ1,subQ0]});Q58=makeQuery(id+"F0.imprint","IMPRINT",FACE,{"disambiguationData":[TD([[makeQuery(id+"F0.imprint","IMPRINT",EDGE,{"disambiguationData":[TD([[subQ2,-1.0]])],"derivedFrom":subQ1}),-1.0]])]});}
            var Q59;
            {var subQ0=sQuery(id+"F0.wireOp",EDGE,"E4.22.1");var subQ1=sQuery(id+"F0.wireOp",EDGE,"E0");var subQ2=makeQuery(id+"F0.imprint","INTERSECT",VERTEX,{"disambiguationData":[OD(0.0)],"derivedFrom":[subQ1,subQ0]});Q59=makeQuery(id+"F0.imprint","IMPRINT",FACE,{"disambiguationData":[TD([[makeQuery(id+"F0.imprint","IMPRINT",EDGE,{"disambiguationData":[TD([[subQ2,-1.0]])],"derivedFrom":subQ1}),-1.0]])]});}
            var Q60;
            {var subQ0=sQuery(id+"F0.wireOp",EDGE,"E4.20.1");var subQ1=sQuery(id+"F0.wireOp",EDGE,"E0");var subQ2=makeQuery(id+"F0.imprint","INTERSECT",VERTEX,{"disambiguationData":[OD(0.0)],"derivedFrom":[subQ1,subQ0]});Q60=makeQuery(id+"F0.imprint","IMPRINT",FACE,{"disambiguationData":[TD([[makeQuery(id+"F0.imprint","IMPRINT",EDGE,{"disambiguationData":[TD([[subQ2,-1.0]])],"derivedFrom":subQ1}),-1.0]])]});}
            var Q61;
            {var subQ0=sQuery(id+"F0.wireOp",EDGE,"E4.34.1");var subQ1=sQuery(id+"F0.wireOp",EDGE,"E0");var subQ2=makeQuery(id+"F0.imprint","INTERSECT",VERTEX,{"disambiguationData":[OD(0.0)],"derivedFrom":[subQ1,subQ0]});Q61=makeQuery(id+"F0.imprint","IMPRINT",FACE,{"disambiguationData":[TD([[makeQuery(id+"F0.imprint","IMPRINT",EDGE,{"disambiguationData":[TD([[subQ2,-1.0]])],"derivedFrom":subQ1}),-1.0]])]});}
            var Q62;
            {var subQ0=sQuery(id+"F0.wireOp",EDGE,"E4.13.1");var subQ1=sQuery(id+"F0.wireOp",EDGE,"E0");var subQ2=makeQuery(id+"F0.imprint","INTERSECT",VERTEX,{"disambiguationData":[OD(0.0)],"derivedFrom":[subQ1,subQ0]});Q62=makeQuery(id+"F0.imprint","IMPRINT",FACE,{"disambiguationData":[TD([[makeQuery(id+"F0.imprint","IMPRINT",EDGE,{"disambiguationData":[TD([[subQ2,-1.0]])],"derivedFrom":subQ1}),1.0]])]});}
            var Q63;
            {var subQ0=sQuery(id+"F0.wireOp",EDGE,"E4.23.1");var subQ1=sQuery(id+"F0.wireOp",EDGE,"E0");var subQ2=makeQuery(id+"F0.imprint","INTERSECT",VERTEX,{"disambiguationData":[OD(0.0)],"derivedFrom":[subQ1,subQ0]});Q63=makeQuery(id+"F0.imprint","IMPRINT",FACE,{"disambiguationData":[TD([[makeQuery(id+"F0.imprint","IMPRINT",EDGE,{"disambiguationData":[TD([[subQ2,-1.0]])],"derivedFrom":subQ1}),1.0]])]});}
            var Q64;
            {var subQ0=sQuery(id+"F0.wireOp",EDGE,"E4.38.1");var subQ1=sQuery(id+"F0.wireOp",EDGE,"E0");var subQ2=makeQuery(id+"F0.imprint","INTERSECT",VERTEX,{"disambiguationData":[OD(0.0)],"derivedFrom":[subQ1,subQ0]});Q64=makeQuery(id+"F0.imprint","IMPRINT",FACE,{"disambiguationData":[TD([[makeQuery(id+"F0.imprint","IMPRINT",EDGE,{"disambiguationData":[TD([[subQ2,-1.0]])],"derivedFrom":subQ1}),-1.0]])]});}
            var Q65;
            {var subQ0=sQuery(id+"F0.wireOp",EDGE,"E4.9.1");var subQ1=sQuery(id+"F0.wireOp",EDGE,"E0");var subQ2=makeQuery(id+"F0.imprint","INTERSECT",VERTEX,{"disambiguationData":[OD(0.0)],"derivedFrom":[subQ1,subQ0]});Q65=makeQuery(id+"F0.imprint","IMPRINT",FACE,{"disambiguationData":[TD([[makeQuery(id+"F0.imprint","IMPRINT",EDGE,{"disambiguationData":[TD([[subQ2,-1.0]])],"derivedFrom":subQ1}),1.0]])]});}
            var Q66;
            {var subQ0=sQuery(id+"F0.wireOp",EDGE,"E4.8.1");var subQ1=sQuery(id+"F0.wireOp",EDGE,"E0");var subQ2=makeQuery(id+"F0.imprint","INTERSECT",VERTEX,{"disambiguationData":[OD(0.0)],"derivedFrom":[subQ1,subQ0]});Q66=makeQuery(id+"F0.imprint","IMPRINT",FACE,{"disambiguationData":[TD([[makeQuery(id+"F0.imprint","IMPRINT",EDGE,{"disambiguationData":[TD([[subQ2,-1.0]])],"derivedFrom":subQ1}),1.0]])]});}
            var Q67;
            {var subQ0=sQuery(id+"F0.wireOp",EDGE,"E4.31.1");var subQ1=sQuery(id+"F0.wireOp",EDGE,"E0");var subQ2=makeQuery(id+"F0.imprint","INTERSECT",VERTEX,{"disambiguationData":[OD(0.0)],"derivedFrom":[subQ1,subQ0]});Q67=makeQuery(id+"F0.imprint","IMPRINT",FACE,{"disambiguationData":[TD([[makeQuery(id+"F0.imprint","IMPRINT",EDGE,{"disambiguationData":[TD([[subQ2,-1.0]])],"derivedFrom":subQ1}),1.0]])]});}
            var Q68;
            {var subQ0=sQuery(id+"F0.wireOp",EDGE,"E4.35.1");var subQ1=sQuery(id+"F0.wireOp",EDGE,"E0");var subQ2=makeQuery(id+"F0.imprint","INTERSECT",VERTEX,{"disambiguationData":[OD(0.0)],"derivedFrom":[subQ1,subQ0]});Q68=makeQuery(id+"F0.imprint","IMPRINT",FACE,{"disambiguationData":[TD([[makeQuery(id+"F0.imprint","IMPRINT",EDGE,{"disambiguationData":[TD([[subQ2,-1.0]])],"derivedFrom":subQ1}),-1.0]])]});}
            var Q69;
            {var subQ0=sQuery(id+"F0.wireOp",EDGE,"E4.17.1");var subQ1=sQuery(id+"F0.wireOp",EDGE,"E0");var subQ2=makeQuery(id+"F0.imprint","INTERSECT",VERTEX,{"disambiguationData":[OD(0.0)],"derivedFrom":[subQ1,subQ0]});Q69=makeQuery(id+"F0.imprint","IMPRINT",FACE,{"disambiguationData":[TD([[makeQuery(id+"F0.imprint","IMPRINT",EDGE,{"disambiguationData":[TD([[subQ2,-1.0]])],"derivedFrom":subQ1}),-1.0]])]});}
            var Q70;
            {var subQ0=sQuery(id+"F0.wireOp",EDGE,"E4.16.1");var subQ1=sQuery(id+"F0.wireOp",EDGE,"E0");var subQ2=makeQuery(id+"F0.imprint","INTERSECT",VERTEX,{"disambiguationData":[OD(0.0)],"derivedFrom":[subQ1,subQ0]});Q70=makeQuery(id+"F0.imprint","IMPRINT",FACE,{"disambiguationData":[TD([[makeQuery(id+"F0.imprint","IMPRINT",EDGE,{"disambiguationData":[TD([[subQ2,-1.0]])],"derivedFrom":subQ1}),-1.0]])]});}
            var Q71;
            {var subQ0=sQuery(id+"F0.wireOp",EDGE,"E4.15.1");var subQ1=sQuery(id+"F0.wireOp",EDGE,"E0");var subQ2=makeQuery(id+"F0.imprint","INTERSECT",VERTEX,{"disambiguationData":[OD(0.0)],"derivedFrom":[subQ1,subQ0]});Q71=makeQuery(id+"F0.imprint","IMPRINT",FACE,{"disambiguationData":[TD([[makeQuery(id+"F0.imprint","IMPRINT",EDGE,{"disambiguationData":[TD([[subQ2,-1.0]])],"derivedFrom":subQ1}),1.0]])]});}
            var Q72;
            {var subQ0=sQuery(id+"F0.wireOp",EDGE,"E4.28.1");var subQ1=sQuery(id+"F0.wireOp",EDGE,"E0");var subQ2=makeQuery(id+"F0.imprint","INTERSECT",VERTEX,{"disambiguationData":[OD(0.0)],"derivedFrom":[subQ1,subQ0]});Q72=makeQuery(id+"F0.imprint","IMPRINT",FACE,{"disambiguationData":[TD([[makeQuery(id+"F0.imprint","IMPRINT",EDGE,{"disambiguationData":[TD([[subQ2,-1.0]])],"derivedFrom":subQ1}),1.0]])]});}
            var Q73;
            {var subQ0=sQuery(id+"F0.wireOp",EDGE,"E4.5.1");var subQ1=sQuery(id+"F0.wireOp",EDGE,"E0");var subQ2=makeQuery(id+"F0.imprint","INTERSECT",VERTEX,{"disambiguationData":[OD(0.0)],"derivedFrom":[subQ1,subQ0]});Q73=makeQuery(id+"F0.imprint","IMPRINT",FACE,{"disambiguationData":[TD([[makeQuery(id+"F0.imprint","IMPRINT",EDGE,{"disambiguationData":[TD([[subQ2,-1.0]])],"derivedFrom":subQ1}),1.0]])]});}
            var Q74;
            {var subQ0=sQuery(id+"F0.wireOp",EDGE,"E4.1.2");var subQ1=sQuery(id+"F0.wireOp",EDGE,"E0");var subQ2=makeQuery(id+"F0.imprint","INTERSECT",VERTEX,{"derivedFrom":[subQ1,subQ0]});Q74=makeQuery(id+"F0.imprint","IMPRINT",FACE,{"disambiguationData":[TD([[makeQuery(id+"F0.imprint","IMPRINT",EDGE,{"disambiguationData":[TD([[subQ2,-1.0]])],"derivedFrom":subQ1}),-1.0]])]});}
            var Q75;
            {var subQ0=sQuery(id+"F0.wireOp",EDGE,"E4.4.1");var subQ1=sQuery(id+"F0.wireOp",EDGE,"E0");var subQ2=makeQuery(id+"F0.imprint","INTERSECT",VERTEX,{"disambiguationData":[OD(0.0)],"derivedFrom":[subQ1,subQ0]});Q75=makeQuery(id+"F0.imprint","IMPRINT",FACE,{"disambiguationData":[TD([[makeQuery(id+"F0.imprint","IMPRINT",EDGE,{"disambiguationData":[TD([[subQ2,-1.0]])],"derivedFrom":subQ1}),-1.0]])]});}
            var Q76;
            {var subQ0=sQuery(id+"F0.wireOp",EDGE,"E4.12.1");var subQ1=sQuery(id+"F0.wireOp",EDGE,"E0");var subQ2=makeQuery(id+"F0.imprint","INTERSECT",VERTEX,{"disambiguationData":[OD(0.0)],"derivedFrom":[subQ1,subQ0]});Q76=makeQuery(id+"F0.imprint","IMPRINT",FACE,{"disambiguationData":[TD([[makeQuery(id+"F0.imprint","IMPRINT",EDGE,{"disambiguationData":[TD([[subQ2,-1.0]])],"derivedFrom":subQ1}),1.0]])]});}
            var Q77;
            {var subQ0=sQuery(id+"F0.wireOp",EDGE,"E4.1.1");var subQ1=sQuery(id+"F0.wireOp",EDGE,"E0");var subQ2=makeQuery(id+"F0.imprint","INTERSECT",VERTEX,{"disambiguationData":[OD(0.0)],"derivedFrom":[subQ1,subQ0]});Q77=makeQuery(id+"F0.imprint","IMPRINT",FACE,{"disambiguationData":[TD([[makeQuery(id+"F0.imprint","IMPRINT",EDGE,{"disambiguationData":[TD([[subQ2,-1.0]])],"derivedFrom":subQ1}),1.0]])]});}
            var Q78;
            {var subQ0=sQuery(id+"F0.wireOp",EDGE,"E4.25.1");var subQ1=sQuery(id+"F0.wireOp",EDGE,"E0");var subQ2=makeQuery(id+"F0.imprint","INTERSECT",VERTEX,{"disambiguationData":[OD(0.0)],"derivedFrom":[subQ1,subQ0]});Q78=makeQuery(id+"F0.imprint","IMPRINT",FACE,{"disambiguationData":[TD([[makeQuery(id+"F0.imprint","IMPRINT",EDGE,{"disambiguationData":[TD([[subQ2,-1.0]])],"derivedFrom":subQ1}),1.0]])]});}
            var Q79;
            {var subQ0=sQuery(id+"F0.wireOp",EDGE,"E4.39.1");var subQ1=sQuery(id+"F0.wireOp",EDGE,"E0");var subQ2=makeQuery(id+"F0.imprint","INTERSECT",VERTEX,{"disambiguationData":[OD(0.0)],"derivedFrom":[subQ1,subQ0]});Q79=makeQuery(id+"F0.imprint","IMPRINT",FACE,{"disambiguationData":[TD([[makeQuery(id+"F0.imprint","IMPRINT",EDGE,{"disambiguationData":[TD([[subQ2,-1.0]])],"derivedFrom":subQ1}),-1.0]])]});}
            var Q80;
            {var subQ0=sQuery(id+"F0.wireOp",EDGE,"E4.27.1");var subQ1=sQuery(id+"F0.wireOp",EDGE,"E0");var subQ2=makeQuery(id+"F0.imprint","INTERSECT",VERTEX,{"disambiguationData":[OD(0.0)],"derivedFrom":[subQ1,subQ0]});Q80=makeQuery(id+"F0.imprint","IMPRINT",FACE,{"disambiguationData":[TD([[makeQuery(id+"F0.imprint","IMPRINT",EDGE,{"disambiguationData":[TD([[subQ2,-1.0]])],"derivedFrom":subQ1}),-1.0]])]});}
            var Q81;
            {var subQ0=sQuery(id+"F0.wireOp",EDGE,"E4.8.1");var subQ1=sQuery(id+"F0.wireOp",EDGE,"E0");var subQ2=makeQuery(id+"F0.imprint","INTERSECT",VERTEX,{"disambiguationData":[OD(0.0)],"derivedFrom":[subQ1,subQ0]});Q81=makeQuery(id+"F0.imprint","IMPRINT",FACE,{"disambiguationData":[TD([[makeQuery(id+"F0.imprint","IMPRINT",EDGE,{"disambiguationData":[TD([[subQ2,-1.0]])],"derivedFrom":subQ1}),-1.0]])]});}
            var Q82;
            {var subQ0=sQuery(id+"F0.wireOp",EDGE,"E4.39.0");var subQ1=sQuery(id+"F0.wireOp",EDGE,"E0");var subQ2=makeQuery(id+"F0.imprint","INTERSECT",VERTEX,{"disambiguationData":[OD(1.0)],"derivedFrom":[subQ1,subQ0]});Q82=makeQuery(id+"F0.imprint","IMPRINT",FACE,{"disambiguationData":[TD([[makeQuery(id+"F0.imprint","IMPRINT",EDGE,{"disambiguationData":[TD([[subQ2,1.0]])],"derivedFrom":subQ1}),-1.0]])]});}
            var Q83;
            {var subQ0=sQuery(id+"F0.wireOp",EDGE,"E4.38.1");var subQ1=sQuery(id+"F0.wireOp",EDGE,"E0");var subQ2=makeQuery(id+"F0.imprint","INTERSECT",VERTEX,{"disambiguationData":[OD(0.0)],"derivedFrom":[subQ1,subQ0]});Q83=makeQuery(id+"F0.imprint","IMPRINT",FACE,{"disambiguationData":[TD([[makeQuery(id+"F0.imprint","IMPRINT",EDGE,{"disambiguationData":[TD([[subQ2,-1.0]])],"derivedFrom":subQ1}),1.0]])]});}
            var Q84;
            {var subQ0=sQuery(id+"F0.wireOp",EDGE,"E1");var subQ1=sQuery(id+"F0.wireOp",EDGE,"E0");var subQ2=makeQuery(id+"F0.imprint","INTERSECT",VERTEX,{"disambiguationData":[OD(0.0)],"derivedFrom":[subQ1,subQ0]});Q84=makeQuery(id+"F0.imprint","IMPRINT",FACE,{"disambiguationData":[TD([[makeQuery(id+"F0.imprint","IMPRINT",EDGE,{"disambiguationData":[TD([[subQ2,-1.0]])],"derivedFrom":subQ1}),-1.0]])]});}
            var Q85;
            {var subQ0=sQuery(id+"F0.wireOp",EDGE,"E4.24.1");var subQ1=sQuery(id+"F0.wireOp",EDGE,"E0");var subQ2=makeQuery(id+"F0.imprint","INTERSECT",VERTEX,{"disambiguationData":[OD(0.0)],"derivedFrom":[subQ1,subQ0]});Q85=makeQuery(id+"F0.imprint","IMPRINT",FACE,{"disambiguationData":[TD([[makeQuery(id+"F0.imprint","IMPRINT",EDGE,{"disambiguationData":[TD([[subQ2,-1.0]])],"derivedFrom":subQ1}),1.0]])]});}
            var Q86;
            {var subQ0=sQuery(id+"F0.wireOp",EDGE,"E4.35.1");var subQ1=sQuery(id+"F0.wireOp",EDGE,"E0");var subQ2=makeQuery(id+"F0.imprint","INTERSECT",VERTEX,{"disambiguationData":[OD(0.0)],"derivedFrom":[subQ1,subQ0]});Q86=makeQuery(id+"F0.imprint","IMPRINT",FACE,{"disambiguationData":[TD([[makeQuery(id+"F0.imprint","IMPRINT",EDGE,{"disambiguationData":[TD([[subQ2,-1.0]])],"derivedFrom":subQ1}),1.0]])]});}
            var Q87;
            {var subQ0=sQuery(id+"F0.wireOp",EDGE,"E4.30.1");var subQ1=sQuery(id+"F0.wireOp",EDGE,"E0");var subQ2=makeQuery(id+"F0.imprint","INTERSECT",VERTEX,{"disambiguationData":[OD(0.0)],"derivedFrom":[subQ1,subQ0]});Q87=makeQuery(id+"F0.imprint","IMPRINT",FACE,{"disambiguationData":[TD([[makeQuery(id+"F0.imprint","IMPRINT",EDGE,{"disambiguationData":[TD([[subQ2,1.0]])],"derivedFrom":subQ1}),-1.0]])]});}
            var Q88;
            {var subQ0=sQuery(id+"F0.wireOp",EDGE,"E4.22.1");var subQ1=sQuery(id+"F0.wireOp",EDGE,"E0");var subQ2=makeQuery(id+"F0.imprint","INTERSECT",VERTEX,{"disambiguationData":[OD(0.0)],"derivedFrom":[subQ1,subQ0]});Q88=makeQuery(id+"F0.imprint","IMPRINT",FACE,{"disambiguationData":[TD([[makeQuery(id+"F0.imprint","IMPRINT",EDGE,{"disambiguationData":[TD([[subQ2,-1.0]])],"derivedFrom":subQ1}),1.0]])]});}
            var Q89;
            {var subQ0=sQuery(id+"F0.wireOp",EDGE,"E3");var subQ1=sQuery(id+"F0.wireOp",EDGE,"E0");var subQ2=makeQuery(id+"F0.imprint","INTERSECT",VERTEX,{"derivedFrom":[subQ1,subQ0]});Q89=makeQuery(id+"F0.imprint","IMPRINT",FACE,{"disambiguationData":[TD([[makeQuery(id+"F0.imprint","IMPRINT",EDGE,{"disambiguationData":[TD([[subQ2,-1.0]])],"derivedFrom":subQ1}),-1.0]])]});}
            var Q90;
            {var subQ0=sQuery(id+"F0.wireOp",EDGE,"E4.24.0");var subQ1=sQuery(id+"F0.wireOp",EDGE,"E0");var subQ2=makeQuery(id+"F0.imprint","INTERSECT",VERTEX,{"disambiguationData":[OD(1.0)],"derivedFrom":[subQ1,subQ0]});Q90=makeQuery(id+"F0.imprint","IMPRINT",FACE,{"disambiguationData":[TD([[makeQuery(id+"F0.imprint","IMPRINT",EDGE,{"disambiguationData":[TD([[subQ2,1.0]])],"derivedFrom":subQ1}),-1.0]])]});}
            var Q91;
            {var subQ0=sQuery(id+"F0.wireOp",EDGE,"E4.27.0");var subQ1=sQuery(id+"F0.wireOp",EDGE,"E0");var subQ2=makeQuery(id+"F0.imprint","INTERSECT",VERTEX,{"disambiguationData":[OD(1.0)],"derivedFrom":[subQ1,subQ0]});Q91=makeQuery(id+"F0.imprint","IMPRINT",FACE,{"disambiguationData":[TD([[makeQuery(id+"F0.imprint","IMPRINT",EDGE,{"disambiguationData":[TD([[subQ2,1.0]])],"derivedFrom":subQ1}),-1.0]])]});}
            var Q92;
            {var subQ0=sQuery(id+"F0.wireOp",EDGE,"E4.21.0");var subQ1=sQuery(id+"F0.wireOp",EDGE,"E0");var subQ2=makeQuery(id+"F0.imprint","INTERSECT",VERTEX,{"disambiguationData":[OD(1.0)],"derivedFrom":[subQ1,subQ0]});Q92=makeQuery(id+"F0.imprint","IMPRINT",FACE,{"disambiguationData":[TD([[makeQuery(id+"F0.imprint","IMPRINT",EDGE,{"disambiguationData":[TD([[subQ2,1.0]])],"derivedFrom":subQ1}),-1.0]])]});}
            var Q93;
            {var subQ0=sQuery(id+"F0.wireOp",EDGE,"E4.2.2");var subQ1=sQuery(id+"F0.wireOp",EDGE,"E0");var subQ2=makeQuery(id+"F0.imprint","INTERSECT",VERTEX,{"derivedFrom":[subQ1,subQ0]});Q93=makeQuery(id+"F0.imprint","IMPRINT",FACE,{"disambiguationData":[TD([[makeQuery(id+"F0.imprint","IMPRINT",EDGE,{"disambiguationData":[TD([[subQ2,-1.0]])],"derivedFrom":subQ1}),-1.0]])]});}
            var Q94;
            {var subQ0=sQuery(id+"F0.wireOp",EDGE,"E2");var subQ1=sQuery(id+"F0.wireOp",EDGE,"E0");var subQ2=makeQuery(id+"F0.imprint","INTERSECT",VERTEX,{"disambiguationData":[OD(0.0)],"derivedFrom":[subQ1,subQ0]});Q94=makeQuery(id+"F0.imprint","IMPRINT",FACE,{"disambiguationData":[TD([[makeQuery(id+"F0.imprint","IMPRINT",EDGE,{"disambiguationData":[TD([[subQ2,1.0]])],"derivedFrom":subQ1}),1.0]])]});}
            var Q95;
            {var subQ0=sQuery(id+"F0.wireOp",EDGE,"E4.38.2");var subQ1=sQuery(id+"F0.wireOp",EDGE,"E0");var subQ2=makeQuery(id+"F0.imprint","INTERSECT",VERTEX,{"derivedFrom":[subQ1,subQ0]});Q95=makeQuery(id+"F0.imprint","IMPRINT",FACE,{"disambiguationData":[TD([[makeQuery(id+"F0.imprint","IMPRINT",EDGE,{"disambiguationData":[TD([[subQ2,-1.0]])],"derivedFrom":subQ1}),-1.0]])]});}
            var Q96;
            {var subQ0=sQuery(id+"F0.wireOp",EDGE,"E4.20.0");var subQ1=sQuery(id+"F0.wireOp",EDGE,"E0");var subQ2=makeQuery(id+"F0.imprint","INTERSECT",VERTEX,{"disambiguationData":[OD(0.0)],"derivedFrom":[subQ1,subQ0]});Q96=makeQuery(id+"F0.imprint","IMPRINT",FACE,{"disambiguationData":[TD([[makeQuery(id+"F0.imprint","IMPRINT",EDGE,{"disambiguationData":[TD([[subQ2,1.0]])],"derivedFrom":subQ1}),1.0]])]});}
            var Q97;
            {var subQ0=sQuery(id+"F0.wireOp",EDGE,"E4.32.0");var subQ1=sQuery(id+"F0.wireOp",EDGE,"E0");var subQ2=makeQuery(id+"F0.imprint","INTERSECT",VERTEX,{"disambiguationData":[OD(1.0)],"derivedFrom":[subQ1,subQ0]});Q97=makeQuery(id+"F0.imprint","IMPRINT",FACE,{"disambiguationData":[TD([[makeQuery(id+"F0.imprint","IMPRINT",EDGE,{"disambiguationData":[TD([[subQ2,1.0]])],"derivedFrom":subQ1}),-1.0]])]});}
            var Q98;
            {var subQ0=sQuery(id+"F0.wireOp",EDGE,"E4.28.0");var subQ1=sQuery(id+"F0.wireOp",EDGE,"E0");var subQ2=makeQuery(id+"F0.imprint","INTERSECT",VERTEX,{"disambiguationData":[OD(1.0)],"derivedFrom":[subQ1,subQ0]});Q98=makeQuery(id+"F0.imprint","IMPRINT",FACE,{"disambiguationData":[TD([[makeQuery(id+"F0.imprint","IMPRINT",EDGE,{"disambiguationData":[TD([[subQ2,1.0]])],"derivedFrom":subQ1}),-1.0]])]});}
            var Q99;
            {var subQ0=sQuery(id+"F0.wireOp",EDGE,"E4.19.0");var subQ1=sQuery(id+"F0.wireOp",EDGE,"E0");var subQ2=makeQuery(id+"F0.imprint","INTERSECT",VERTEX,{"disambiguationData":[OD(0.0)],"derivedFrom":[subQ1,subQ0]});Q99=makeQuery(id+"F0.imprint","IMPRINT",FACE,{"disambiguationData":[TD([[makeQuery(id+"F0.imprint","IMPRINT",EDGE,{"disambiguationData":[TD([[subQ2,1.0]])],"derivedFrom":subQ1}),1.0]])]});}
            var Q100;
            {var subQ0=sQuery(id+"F0.wireOp",EDGE,"E4.37.0");var subQ1=sQuery(id+"F0.wireOp",EDGE,"E0");var subQ2=makeQuery(id+"F0.imprint","INTERSECT",VERTEX,{"disambiguationData":[OD(0.0)],"derivedFrom":[subQ1,subQ0]});Q100=makeQuery(id+"F0.imprint","IMPRINT",FACE,{"disambiguationData":[TD([[makeQuery(id+"F0.imprint","IMPRINT",EDGE,{"disambiguationData":[TD([[subQ2,1.0]])],"derivedFrom":subQ1}),1.0]])]});}
            var Q101;
            {var subQ0=sQuery(id+"F0.wireOp",EDGE,"E4.12.0");var subQ1=sQuery(id+"F0.wireOp",EDGE,"E0");var subQ2=makeQuery(id+"F0.imprint","INTERSECT",VERTEX,{"disambiguationData":[OD(1.0)],"derivedFrom":[subQ1,subQ0]});Q101=makeQuery(id+"F0.imprint","IMPRINT",FACE,{"disambiguationData":[TD([[makeQuery(id+"F0.imprint","IMPRINT",EDGE,{"disambiguationData":[TD([[subQ2,1.0]])],"derivedFrom":subQ1}),-1.0]])]});}
            var Q102;
            {var subQ0=sQuery(id+"F0.wireOp",EDGE,"E4.35.2");var subQ1=sQuery(id+"F0.wireOp",EDGE,"E0");var subQ2=makeQuery(id+"F0.imprint","INTERSECT",VERTEX,{"derivedFrom":[subQ1,subQ0]});Q102=makeQuery(id+"F0.imprint","IMPRINT",FACE,{"disambiguationData":[TD([[makeQuery(id+"F0.imprint","IMPRINT",EDGE,{"disambiguationData":[TD([[subQ2,-1.0]])],"derivedFrom":subQ1}),-1.0]])]});}
            var Q103;
            {var subQ0=sQuery(id+"F0.wireOp",EDGE,"E4.12.2");var subQ1=sQuery(id+"F0.wireOp",EDGE,"E0");var subQ2=makeQuery(id+"F0.imprint","INTERSECT",VERTEX,{"derivedFrom":[subQ1,subQ0]});Q103=makeQuery(id+"F0.imprint","IMPRINT",FACE,{"disambiguationData":[TD([[makeQuery(id+"F0.imprint","IMPRINT",EDGE,{"disambiguationData":[TD([[subQ2,-1.0]])],"derivedFrom":subQ1}),-1.0]])]});}
            var Q104;
            {var subQ0=sQuery(id+"F0.wireOp",EDGE,"E4.4.0");var subQ1=sQuery(id+"F0.wireOp",EDGE,"E0");var subQ2=makeQuery(id+"F0.imprint","INTERSECT",VERTEX,{"disambiguationData":[OD(0.0)],"derivedFrom":[subQ1,subQ0]});Q104=makeQuery(id+"F0.imprint","IMPRINT",FACE,{"disambiguationData":[TD([[makeQuery(id+"F0.imprint","IMPRINT",EDGE,{"disambiguationData":[TD([[subQ2,1.0]])],"derivedFrom":subQ1}),1.0]])]});}
            var Q105;
            {var subQ0=sQuery(id+"F0.wireOp",EDGE,"E4.9.0");var subQ1=sQuery(id+"F0.wireOp",EDGE,"E0");var subQ2=makeQuery(id+"F0.imprint","INTERSECT",VERTEX,{"disambiguationData":[OD(0.0)],"derivedFrom":[subQ1,subQ0]});Q105=makeQuery(id+"F0.imprint","IMPRINT",FACE,{"disambiguationData":[TD([[makeQuery(id+"F0.imprint","IMPRINT",EDGE,{"disambiguationData":[TD([[subQ2,1.0]])],"derivedFrom":subQ1}),1.0]])]});}
            var Q106;
            {var subQ0=sQuery(id+"F0.wireOp",EDGE,"E4.36.0");var subQ1=sQuery(id+"F0.wireOp",EDGE,"E0");var subQ2=makeQuery(id+"F0.imprint","INTERSECT",VERTEX,{"disambiguationData":[OD(0.0)],"derivedFrom":[subQ1,subQ0]});Q106=makeQuery(id+"F0.imprint","IMPRINT",FACE,{"disambiguationData":[TD([[makeQuery(id+"F0.imprint","IMPRINT",EDGE,{"disambiguationData":[TD([[subQ2,1.0]])],"derivedFrom":subQ1}),1.0]])]});}
            var Q107;
            {var subQ0=sQuery(id+"F0.wireOp",EDGE,"E4.18.0");var subQ1=sQuery(id+"F0.wireOp",EDGE,"E0");var subQ2=makeQuery(id+"F0.imprint","INTERSECT",VERTEX,{"disambiguationData":[OD(1.0)],"derivedFrom":[subQ1,subQ0]});Q107=makeQuery(id+"F0.imprint","IMPRINT",FACE,{"disambiguationData":[TD([[makeQuery(id+"F0.imprint","IMPRINT",EDGE,{"disambiguationData":[TD([[subQ2,1.0]])],"derivedFrom":subQ1}),-1.0]])]});}
            var Q108;
            {var subQ0=sQuery(id+"F0.wireOp",EDGE,"E4.23.2");var subQ1=sQuery(id+"F0.wireOp",EDGE,"E0");var subQ2=makeQuery(id+"F0.imprint","INTERSECT",VERTEX,{"derivedFrom":[subQ1,subQ0]});Q108=makeQuery(id+"F0.imprint","IMPRINT",FACE,{"disambiguationData":[TD([[makeQuery(id+"F0.imprint","IMPRINT",EDGE,{"disambiguationData":[TD([[subQ2,-1.0]])],"derivedFrom":subQ1}),-1.0]])]});}
            var Q109;
            {var subQ0=sQuery(id+"F0.wireOp",EDGE,"E4.6.0");var subQ1=sQuery(id+"F0.wireOp",EDGE,"E0");var subQ2=makeQuery(id+"F0.imprint","INTERSECT",VERTEX,{"disambiguationData":[OD(0.0)],"derivedFrom":[subQ1,subQ0]});Q109=makeQuery(id+"F0.imprint","IMPRINT",FACE,{"disambiguationData":[TD([[makeQuery(id+"F0.imprint","IMPRINT",EDGE,{"disambiguationData":[TD([[subQ2,1.0]])],"derivedFrom":subQ1}),1.0]])]});}
            var Q110;
            {var subQ0=sQuery(id+"F0.wireOp",EDGE,"E4.3.2");var subQ1=sQuery(id+"F0.wireOp",EDGE,"E0");var subQ2=makeQuery(id+"F0.imprint","INTERSECT",VERTEX,{"derivedFrom":[subQ1,subQ0]});Q110=makeQuery(id+"F0.imprint","IMPRINT",FACE,{"disambiguationData":[TD([[makeQuery(id+"F0.imprint","IMPRINT",EDGE,{"disambiguationData":[TD([[subQ2,-1.0]])],"derivedFrom":subQ1}),-1.0]])]});}
            var Q111;
            {var subQ0=sQuery(id+"F0.wireOp",EDGE,"E4.32.2");var subQ1=sQuery(id+"F0.wireOp",EDGE,"E0");var subQ2=makeQuery(id+"F0.imprint","INTERSECT",VERTEX,{"derivedFrom":[subQ1,subQ0]});Q111=makeQuery(id+"F0.imprint","IMPRINT",FACE,{"disambiguationData":[TD([[makeQuery(id+"F0.imprint","IMPRINT",EDGE,{"disambiguationData":[TD([[subQ2,-1.0]])],"derivedFrom":subQ1}),-1.0]])]});}
            var Q112;
            {var subQ0=sQuery(id+"F0.wireOp",EDGE,"E4.34.0");var subQ1=sQuery(id+"F0.wireOp",EDGE,"E0");var subQ2=makeQuery(id+"F0.imprint","INTERSECT",VERTEX,{"disambiguationData":[OD(0.0)],"derivedFrom":[subQ1,subQ0]});Q112=makeQuery(id+"F0.imprint","IMPRINT",FACE,{"disambiguationData":[TD([[makeQuery(id+"F0.imprint","IMPRINT",EDGE,{"disambiguationData":[TD([[subQ2,1.0]])],"derivedFrom":subQ1}),1.0]])]});}
            var Q113;
            {var subQ0=sQuery(id+"F0.wireOp",EDGE,"E4.22.2");var subQ1=sQuery(id+"F0.wireOp",EDGE,"E0");var subQ2=makeQuery(id+"F0.imprint","INTERSECT",VERTEX,{"derivedFrom":[subQ1,subQ0]});Q113=makeQuery(id+"F0.imprint","IMPRINT",FACE,{"disambiguationData":[TD([[makeQuery(id+"F0.imprint","IMPRINT",EDGE,{"disambiguationData":[TD([[subQ2,-1.0]])],"derivedFrom":subQ1}),-1.0]])]});}
            var Q114;
            {var subQ0=sQuery(id+"F0.wireOp",EDGE,"E4.26.0");var subQ1=sQuery(id+"F0.wireOp",EDGE,"E0");var subQ2=makeQuery(id+"F0.imprint","INTERSECT",VERTEX,{"disambiguationData":[OD(0.0)],"derivedFrom":[subQ1,subQ0]});Q114=makeQuery(id+"F0.imprint","IMPRINT",FACE,{"disambiguationData":[TD([[makeQuery(id+"F0.imprint","IMPRINT",EDGE,{"disambiguationData":[TD([[subQ2,1.0]])],"derivedFrom":subQ1}),1.0]])]});}
            var Q115;
            {var subQ0=sQuery(id+"F0.wireOp",EDGE,"E4.24.0");var subQ1=sQuery(id+"F0.wireOp",EDGE,"E0");var subQ2=makeQuery(id+"F0.imprint","INTERSECT",VERTEX,{"disambiguationData":[OD(0.0)],"derivedFrom":[subQ1,subQ0]});Q115=makeQuery(id+"F0.imprint","IMPRINT",FACE,{"disambiguationData":[TD([[makeQuery(id+"F0.imprint","IMPRINT",EDGE,{"disambiguationData":[TD([[subQ2,1.0]])],"derivedFrom":subQ1}),1.0]])]});}
            var Q116;
            {var subQ0=sQuery(id+"F0.wireOp",EDGE,"E4.15.0");var subQ1=sQuery(id+"F0.wireOp",EDGE,"E0");var subQ2=makeQuery(id+"F0.imprint","INTERSECT",VERTEX,{"disambiguationData":[OD(0.0)],"derivedFrom":[subQ1,subQ0]});Q116=makeQuery(id+"F0.imprint","IMPRINT",FACE,{"disambiguationData":[TD([[makeQuery(id+"F0.imprint","IMPRINT",EDGE,{"disambiguationData":[TD([[subQ2,1.0]])],"derivedFrom":subQ1}),1.0]])]});}
            var Q117;
            {var subQ0=sQuery(id+"F0.wireOp",EDGE,"E4.36.0");var subQ1=sQuery(id+"F0.wireOp",EDGE,"E0");var subQ2=makeQuery(id+"F0.imprint","INTERSECT",VERTEX,{"disambiguationData":[OD(1.0)],"derivedFrom":[subQ1,subQ0]});Q117=makeQuery(id+"F0.imprint","IMPRINT",FACE,{"disambiguationData":[TD([[makeQuery(id+"F0.imprint","IMPRINT",EDGE,{"disambiguationData":[TD([[subQ2,1.0]])],"derivedFrom":subQ1}),-1.0]])]});}
            var Q118;
            {var subQ0=sQuery(id+"F0.wireOp",EDGE,"E4.21.2");var subQ1=sQuery(id+"F0.wireOp",EDGE,"E0");var subQ2=makeQuery(id+"F0.imprint","INTERSECT",VERTEX,{"derivedFrom":[subQ1,subQ0]});Q118=makeQuery(id+"F0.imprint","IMPRINT",FACE,{"disambiguationData":[TD([[makeQuery(id+"F0.imprint","IMPRINT",EDGE,{"disambiguationData":[TD([[subQ2,-1.0]])],"derivedFrom":subQ1}),-1.0]])]});}
            var Q119;
            {var subQ0=sQuery(id+"F0.wireOp",EDGE,"E4.8.2");var subQ1=sQuery(id+"F0.wireOp",EDGE,"E0");var subQ2=makeQuery(id+"F0.imprint","INTERSECT",VERTEX,{"derivedFrom":[subQ1,subQ0]});Q119=makeQuery(id+"F0.imprint","IMPRINT",FACE,{"disambiguationData":[TD([[makeQuery(id+"F0.imprint","IMPRINT",EDGE,{"disambiguationData":[TD([[subQ2,-1.0]])],"derivedFrom":subQ1}),-1.0]])]});}
            var Q120;
            {var subQ0=sQuery(id+"F0.wireOp",EDGE,"E4.39.0");var subQ1=sQuery(id+"F0.wireOp",EDGE,"E0");var subQ2=makeQuery(id+"F0.imprint","INTERSECT",VERTEX,{"disambiguationData":[OD(0.0)],"derivedFrom":[subQ1,subQ0]});Q120=makeQuery(id+"F0.imprint","IMPRINT",FACE,{"disambiguationData":[TD([[makeQuery(id+"F0.imprint","IMPRINT",EDGE,{"disambiguationData":[TD([[subQ2,1.0]])],"derivedFrom":subQ1}),1.0]])]});}
            var Q121;
            {var subQ0=sQuery(id+"F0.wireOp",EDGE,"E4.14.2");var subQ1=sQuery(id+"F0.wireOp",EDGE,"E0");var subQ2=makeQuery(id+"F0.imprint","INTERSECT",VERTEX,{"derivedFrom":[subQ1,subQ0]});Q121=makeQuery(id+"F0.imprint","IMPRINT",FACE,{"disambiguationData":[TD([[makeQuery(id+"F0.imprint","IMPRINT",EDGE,{"disambiguationData":[TD([[subQ2,-1.0]])],"derivedFrom":subQ1}),-1.0]])]});}
            var Q122;
            {var subQ0=sQuery(id+"F0.wireOp",EDGE,"E4.22.0");var subQ1=sQuery(id+"F0.wireOp",EDGE,"E0");var subQ2=makeQuery(id+"F0.imprint","INTERSECT",VERTEX,{"disambiguationData":[OD(1.0)],"derivedFrom":[subQ1,subQ0]});Q122=makeQuery(id+"F0.imprint","IMPRINT",FACE,{"disambiguationData":[TD([[makeQuery(id+"F0.imprint","IMPRINT",EDGE,{"disambiguationData":[TD([[subQ2,1.0]])],"derivedFrom":subQ1}),-1.0]])]});}
            var Q123;
            {var subQ0=sQuery(id+"F0.wireOp",EDGE,"E4.33.0");var subQ1=sQuery(id+"F0.wireOp",EDGE,"E0");var subQ2=makeQuery(id+"F0.imprint","INTERSECT",VERTEX,{"disambiguationData":[OD(0.0)],"derivedFrom":[subQ1,subQ0]});Q123=makeQuery(id+"F0.imprint","IMPRINT",FACE,{"disambiguationData":[TD([[makeQuery(id+"F0.imprint","IMPRINT",EDGE,{"disambiguationData":[TD([[subQ2,1.0]])],"derivedFrom":subQ1}),1.0]])]});}
            var Q124;
            {var subQ0=sQuery(id+"F0.wireOp",EDGE,"E4.5.2");var subQ1=sQuery(id+"F0.wireOp",EDGE,"E0");var subQ2=makeQuery(id+"F0.imprint","INTERSECT",VERTEX,{"derivedFrom":[subQ1,subQ0]});Q124=makeQuery(id+"F0.imprint","IMPRINT",FACE,{"disambiguationData":[TD([[makeQuery(id+"F0.imprint","IMPRINT",EDGE,{"disambiguationData":[TD([[subQ2,-1.0]])],"derivedFrom":subQ1}),-1.0]])]});}
            var Q125;
            {var subQ0=sQuery(id+"F0.wireOp",EDGE,"E4.13.0");var subQ1=sQuery(id+"F0.wireOp",EDGE,"E0");var subQ2=makeQuery(id+"F0.imprint","INTERSECT",VERTEX,{"disambiguationData":[OD(1.0)],"derivedFrom":[subQ1,subQ0]});Q125=makeQuery(id+"F0.imprint","IMPRINT",FACE,{"disambiguationData":[TD([[makeQuery(id+"F0.imprint","IMPRINT",EDGE,{"disambiguationData":[TD([[subQ2,1.0]])],"derivedFrom":subQ1}),-1.0]])]});}
            var Q126;
            {var subQ0=sQuery(id+"F0.wireOp",EDGE,"E4.5.0");var subQ1=sQuery(id+"F0.wireOp",EDGE,"E0");var subQ2=makeQuery(id+"F0.imprint","INTERSECT",VERTEX,{"disambiguationData":[OD(0.0)],"derivedFrom":[subQ1,subQ0]});Q126=makeQuery(id+"F0.imprint","IMPRINT",FACE,{"disambiguationData":[TD([[makeQuery(id+"F0.imprint","IMPRINT",EDGE,{"disambiguationData":[TD([[subQ2,1.0]])],"derivedFrom":subQ1}),1.0]])]});}
            var Q127;
            {var subQ0=sQuery(id+"F0.wireOp",EDGE,"E4.14.0");var subQ1=sQuery(id+"F0.wireOp",EDGE,"E0");var subQ2=makeQuery(id+"F0.imprint","INTERSECT",VERTEX,{"disambiguationData":[OD(1.0)],"derivedFrom":[subQ1,subQ0]});Q127=makeQuery(id+"F0.imprint","IMPRINT",FACE,{"disambiguationData":[TD([[makeQuery(id+"F0.imprint","IMPRINT",EDGE,{"disambiguationData":[TD([[subQ2,1.0]])],"derivedFrom":subQ1}),-1.0]])]});}
            var Q128;
            {var subQ0=sQuery(id+"F0.wireOp",EDGE,"E4.35.0");var subQ1=sQuery(id+"F0.wireOp",EDGE,"E0");var subQ2=makeQuery(id+"F0.imprint","INTERSECT",VERTEX,{"disambiguationData":[OD(0.0)],"derivedFrom":[subQ1,subQ0]});Q128=makeQuery(id+"F0.imprint","IMPRINT",FACE,{"disambiguationData":[TD([[makeQuery(id+"F0.imprint","IMPRINT",EDGE,{"disambiguationData":[TD([[subQ2,1.0]])],"derivedFrom":subQ1}),1.0]])]});}
            var Q129;
            {var subQ0=sQuery(id+"F0.wireOp",EDGE,"E4.4.2");var subQ1=sQuery(id+"F0.wireOp",EDGE,"E0");var subQ2=makeQuery(id+"F0.imprint","INTERSECT",VERTEX,{"derivedFrom":[subQ1,subQ0]});Q129=makeQuery(id+"F0.imprint","IMPRINT",FACE,{"disambiguationData":[TD([[makeQuery(id+"F0.imprint","IMPRINT",EDGE,{"disambiguationData":[TD([[subQ2,-1.0]])],"derivedFrom":subQ1}),-1.0]])]});}
            var Q130;
            {var subQ0=sQuery(id+"F0.wireOp",EDGE,"E4.18.2");var subQ1=sQuery(id+"F0.wireOp",EDGE,"E0");var subQ2=makeQuery(id+"F0.imprint","INTERSECT",VERTEX,{"derivedFrom":[subQ1,subQ0]});Q130=makeQuery(id+"F0.imprint","IMPRINT",FACE,{"disambiguationData":[TD([[makeQuery(id+"F0.imprint","IMPRINT",EDGE,{"disambiguationData":[TD([[subQ2,-1.0]])],"derivedFrom":subQ1}),-1.0]])]});}
            var Q131;
            {var subQ0=sQuery(id+"F0.wireOp",EDGE,"E4.10.0");var subQ1=sQuery(id+"F0.wireOp",EDGE,"E0");var subQ2=makeQuery(id+"F0.imprint","INTERSECT",VERTEX,{"disambiguationData":[OD(0.0)],"derivedFrom":[subQ1,subQ0]});Q131=makeQuery(id+"F0.imprint","IMPRINT",FACE,{"disambiguationData":[TD([[makeQuery(id+"F0.imprint","IMPRINT",EDGE,{"disambiguationData":[TD([[subQ2,1.0]])],"derivedFrom":subQ1}),1.0]])]});}
            var Q132;
            {var subQ0=sQuery(id+"F0.wireOp",EDGE,"E4.37.0");var subQ1=sQuery(id+"F0.wireOp",EDGE,"E0");var subQ2=makeQuery(id+"F0.imprint","INTERSECT",VERTEX,{"disambiguationData":[OD(1.0)],"derivedFrom":[subQ1,subQ0]});Q132=makeQuery(id+"F0.imprint","IMPRINT",FACE,{"disambiguationData":[TD([[makeQuery(id+"F0.imprint","IMPRINT",EDGE,{"disambiguationData":[TD([[subQ2,1.0]])],"derivedFrom":subQ1}),-1.0]])]});}
            var Q133;
            {var subQ0=sQuery(id+"F0.wireOp",EDGE,"E4.3.0");var subQ1=sQuery(id+"F0.wireOp",EDGE,"E0");var subQ2=makeQuery(id+"F0.imprint","INTERSECT",VERTEX,{"disambiguationData":[OD(1.0)],"derivedFrom":[subQ1,subQ0]});Q133=makeQuery(id+"F0.imprint","IMPRINT",FACE,{"disambiguationData":[TD([[makeQuery(id+"F0.imprint","IMPRINT",EDGE,{"disambiguationData":[TD([[subQ2,1.0]])],"derivedFrom":subQ1}),-1.0]])]});}
            var Q134;
            {var subQ0=sQuery(id+"F0.wireOp",EDGE,"E4.10.2");var subQ1=sQuery(id+"F0.wireOp",EDGE,"E0");var subQ2=makeQuery(id+"F0.imprint","INTERSECT",VERTEX,{"derivedFrom":[subQ1,subQ0]});Q134=makeQuery(id+"F0.imprint","IMPRINT",FACE,{"disambiguationData":[TD([[makeQuery(id+"F0.imprint","IMPRINT",EDGE,{"disambiguationData":[TD([[subQ2,-1.0]])],"derivedFrom":subQ1}),-1.0]])]});}
            var Q135;
            {var subQ0=sQuery(id+"F0.wireOp",EDGE,"E4.7.0");var subQ1=sQuery(id+"F0.wireOp",EDGE,"E0");var subQ2=makeQuery(id+"F0.imprint","INTERSECT",VERTEX,{"disambiguationData":[OD(1.0)],"derivedFrom":[subQ1,subQ0]});Q135=makeQuery(id+"F0.imprint","IMPRINT",FACE,{"disambiguationData":[TD([[makeQuery(id+"F0.imprint","IMPRINT",EDGE,{"disambiguationData":[TD([[subQ2,1.0]])],"derivedFrom":subQ1}),-1.0]])]});}
            var Q136;
            {var subQ0=sQuery(id+"F0.wireOp",EDGE,"E4.6.0");var subQ1=sQuery(id+"F0.wireOp",EDGE,"E0");var subQ2=makeQuery(id+"F0.imprint","INTERSECT",VERTEX,{"disambiguationData":[OD(1.0)],"derivedFrom":[subQ1,subQ0]});Q136=makeQuery(id+"F0.imprint","IMPRINT",FACE,{"disambiguationData":[TD([[makeQuery(id+"F0.imprint","IMPRINT",EDGE,{"disambiguationData":[TD([[subQ2,1.0]])],"derivedFrom":subQ1}),-1.0]])]});}
            var Q137;
            {var subQ0=sQuery(id+"F0.wireOp",EDGE,"E4.2.0");var subQ1=sQuery(id+"F0.wireOp",EDGE,"E0");var subQ2=makeQuery(id+"F0.imprint","INTERSECT",VERTEX,{"disambiguationData":[OD(1.0)],"derivedFrom":[subQ1,subQ0]});Q137=makeQuery(id+"F0.imprint","IMPRINT",FACE,{"disambiguationData":[TD([[makeQuery(id+"F0.imprint","IMPRINT",EDGE,{"disambiguationData":[TD([[subQ2,1.0]])],"derivedFrom":subQ1}),-1.0]])]});}
            var Q138;
            {var subQ0=sQuery(id+"F0.wireOp",EDGE,"E4.33.0");var subQ1=sQuery(id+"F0.wireOp",EDGE,"E0");var subQ2=makeQuery(id+"F0.imprint","INTERSECT",VERTEX,{"disambiguationData":[OD(1.0)],"derivedFrom":[subQ1,subQ0]});Q138=makeQuery(id+"F0.imprint","IMPRINT",FACE,{"disambiguationData":[TD([[makeQuery(id+"F0.imprint","IMPRINT",EDGE,{"disambiguationData":[TD([[subQ2,1.0]])],"derivedFrom":subQ1}),-1.0]])]});}
            var Q139;
            {var subQ0=sQuery(id+"F0.wireOp",EDGE,"E4.10.0");var subQ1=sQuery(id+"F0.wireOp",EDGE,"E0");var subQ2=makeQuery(id+"F0.imprint","INTERSECT",VERTEX,{"disambiguationData":[OD(1.0)],"derivedFrom":[subQ1,subQ0]});Q139=makeQuery(id+"F0.imprint","IMPRINT",FACE,{"disambiguationData":[TD([[makeQuery(id+"F0.imprint","IMPRINT",EDGE,{"disambiguationData":[TD([[subQ2,1.0]])],"derivedFrom":subQ1}),-1.0]])]});}
            var Q140;
            {var subQ0=sQuery(id+"F0.wireOp",EDGE,"E4.16.0");var subQ1=sQuery(id+"F0.wireOp",EDGE,"E0");var subQ2=makeQuery(id+"F0.imprint","INTERSECT",VERTEX,{"disambiguationData":[OD(0.0)],"derivedFrom":[subQ1,subQ0]});Q140=makeQuery(id+"F0.imprint","IMPRINT",FACE,{"disambiguationData":[TD([[makeQuery(id+"F0.imprint","IMPRINT",EDGE,{"disambiguationData":[TD([[subQ2,1.0]])],"derivedFrom":subQ1}),1.0]])]});}
            var Q141;
            {var subQ0=sQuery(id+"F0.wireOp",EDGE,"E4.19.0");var subQ1=sQuery(id+"F0.wireOp",EDGE,"E0");var subQ2=makeQuery(id+"F0.imprint","INTERSECT",VERTEX,{"disambiguationData":[OD(1.0)],"derivedFrom":[subQ1,subQ0]});Q141=makeQuery(id+"F0.imprint","IMPRINT",FACE,{"disambiguationData":[TD([[makeQuery(id+"F0.imprint","IMPRINT",EDGE,{"disambiguationData":[TD([[subQ2,1.0]])],"derivedFrom":subQ1}),-1.0]])]});}
            var Q142;
            {var subQ0=sQuery(id+"F0.wireOp",EDGE,"E4.29.0");var subQ1=sQuery(id+"F0.wireOp",EDGE,"E0");var subQ2=makeQuery(id+"F0.imprint","INTERSECT",VERTEX,{"disambiguationData":[OD(1.0)],"derivedFrom":[subQ1,subQ0]});Q142=makeQuery(id+"F0.imprint","IMPRINT",FACE,{"disambiguationData":[TD([[makeQuery(id+"F0.imprint","IMPRINT",EDGE,{"disambiguationData":[TD([[subQ2,1.0]])],"derivedFrom":subQ1}),-1.0]])]});}
            var Q143;
            {var subQ0=sQuery(id+"F0.wireOp",EDGE,"E4.31.0");var subQ1=sQuery(id+"F0.wireOp",EDGE,"E0");var subQ2=makeQuery(id+"F0.imprint","INTERSECT",VERTEX,{"disambiguationData":[OD(0.0)],"derivedFrom":[subQ1,subQ0]});Q143=makeQuery(id+"F0.imprint","IMPRINT",FACE,{"disambiguationData":[TD([[makeQuery(id+"F0.imprint","IMPRINT",EDGE,{"disambiguationData":[TD([[subQ2,1.0]])],"derivedFrom":subQ1}),1.0]])]});}
            var Q144;
            {var subQ0=sQuery(id+"F0.wireOp",EDGE,"E4.30.0");var subQ1=sQuery(id+"F0.wireOp",EDGE,"E0");var subQ2=makeQuery(id+"F0.imprint","INTERSECT",VERTEX,{"disambiguationData":[OD(0.0)],"derivedFrom":[subQ1,subQ0]});Q144=makeQuery(id+"F0.imprint","IMPRINT",FACE,{"disambiguationData":[TD([[makeQuery(id+"F0.imprint","IMPRINT",EDGE,{"disambiguationData":[TD([[subQ2,1.0]])],"derivedFrom":subQ1}),1.0]])]});}
            var Q145;
            {var subQ0=sQuery(id+"F0.wireOp",EDGE,"E4.3.0");var subQ1=sQuery(id+"F0.wireOp",EDGE,"E0");var subQ2=makeQuery(id+"F0.imprint","INTERSECT",VERTEX,{"disambiguationData":[OD(0.0)],"derivedFrom":[subQ1,subQ0]});Q145=makeQuery(id+"F0.imprint","IMPRINT",FACE,{"disambiguationData":[TD([[makeQuery(id+"F0.imprint","IMPRINT",EDGE,{"disambiguationData":[TD([[subQ2,1.0]])],"derivedFrom":subQ1}),1.0]])]});}
            var Q146;
            {var subQ0=sQuery(id+"F0.wireOp",EDGE,"E4.9.2");var subQ1=sQuery(id+"F0.wireOp",EDGE,"E0");var subQ2=makeQuery(id+"F0.imprint","INTERSECT",VERTEX,{"derivedFrom":[subQ1,subQ0]});Q146=makeQuery(id+"F0.imprint","IMPRINT",FACE,{"disambiguationData":[TD([[makeQuery(id+"F0.imprint","IMPRINT",EDGE,{"disambiguationData":[TD([[subQ2,-1.0]])],"derivedFrom":subQ1}),-1.0]])]});}
            var Q147;
            {var subQ0=sQuery(id+"F0.wireOp",EDGE,"E2");var subQ1=sQuery(id+"F0.wireOp",EDGE,"E0");var subQ2=makeQuery(id+"F0.imprint","INTERSECT",VERTEX,{"disambiguationData":[OD(1.0)],"derivedFrom":[subQ1,subQ0]});Q147=makeQuery(id+"F0.imprint","IMPRINT",FACE,{"disambiguationData":[TD([[makeQuery(id+"F0.imprint","IMPRINT",EDGE,{"disambiguationData":[TD([[subQ2,1.0]])],"derivedFrom":subQ1}),-1.0]])]});}
            var Q148;
            {var subQ0=sQuery(id+"F0.wireOp",EDGE,"E4.4.0");var subQ1=sQuery(id+"F0.wireOp",EDGE,"E0");var subQ2=makeQuery(id+"F0.imprint","INTERSECT",VERTEX,{"disambiguationData":[OD(1.0)],"derivedFrom":[subQ1,subQ0]});Q148=makeQuery(id+"F0.imprint","IMPRINT",FACE,{"disambiguationData":[TD([[makeQuery(id+"F0.imprint","IMPRINT",EDGE,{"disambiguationData":[TD([[subQ2,1.0]])],"derivedFrom":subQ1}),-1.0]])]});}
            var Q149;
            {var subQ0=sQuery(id+"F0.wireOp",EDGE,"E4.24.2");var subQ1=sQuery(id+"F0.wireOp",EDGE,"E0");var subQ2=makeQuery(id+"F0.imprint","INTERSECT",VERTEX,{"derivedFrom":[subQ1,subQ0]});Q149=makeQuery(id+"F0.imprint","IMPRINT",FACE,{"disambiguationData":[TD([[makeQuery(id+"F0.imprint","IMPRINT",EDGE,{"disambiguationData":[TD([[subQ2,-1.0]])],"derivedFrom":subQ1}),-1.0]])]});}
            var Q150;
            {var subQ0=sQuery(id+"F0.wireOp",EDGE,"E4.26.2");var subQ1=sQuery(id+"F0.wireOp",EDGE,"E0");var subQ2=makeQuery(id+"F0.imprint","INTERSECT",VERTEX,{"derivedFrom":[subQ1,subQ0]});Q150=makeQuery(id+"F0.imprint","IMPRINT",FACE,{"disambiguationData":[TD([[makeQuery(id+"F0.imprint","IMPRINT",EDGE,{"disambiguationData":[TD([[subQ2,-1.0]])],"derivedFrom":subQ1}),-1.0]])]});}
            var Q151;
            {var subQ0=sQuery(id+"F0.wireOp",EDGE,"E4.27.2");var subQ1=sQuery(id+"F0.wireOp",EDGE,"E0");var subQ2=makeQuery(id+"F0.imprint","INTERSECT",VERTEX,{"derivedFrom":[subQ1,subQ0]});Q151=makeQuery(id+"F0.imprint","IMPRINT",FACE,{"disambiguationData":[TD([[makeQuery(id+"F0.imprint","IMPRINT",EDGE,{"disambiguationData":[TD([[subQ2,-1.0]])],"derivedFrom":subQ1}),-1.0]])]});}
            var Q152;
            {var subQ0=sQuery(id+"F0.wireOp",EDGE,"E4.9.0");var subQ1=sQuery(id+"F0.wireOp",EDGE,"E0");var subQ2=makeQuery(id+"F0.imprint","INTERSECT",VERTEX,{"disambiguationData":[OD(1.0)],"derivedFrom":[subQ1,subQ0]});Q152=makeQuery(id+"F0.imprint","IMPRINT",FACE,{"disambiguationData":[TD([[makeQuery(id+"F0.imprint","IMPRINT",EDGE,{"disambiguationData":[TD([[subQ2,1.0]])],"derivedFrom":subQ1}),-1.0]])]});}
            var Q153;
            {var subQ0=sQuery(id+"F0.wireOp",EDGE,"E4.13.2");var subQ1=sQuery(id+"F0.wireOp",EDGE,"E0");var subQ2=makeQuery(id+"F0.imprint","INTERSECT",VERTEX,{"derivedFrom":[subQ1,subQ0]});Q153=makeQuery(id+"F0.imprint","IMPRINT",FACE,{"disambiguationData":[TD([[makeQuery(id+"F0.imprint","IMPRINT",EDGE,{"disambiguationData":[TD([[subQ2,-1.0]])],"derivedFrom":subQ1}),-1.0]])]});}
            var Q154;
            {var subQ0=sQuery(id+"F0.wireOp",EDGE,"E4.15.2");var subQ1=sQuery(id+"F0.wireOp",EDGE,"E0");var subQ2=makeQuery(id+"F0.imprint","INTERSECT",VERTEX,{"derivedFrom":[subQ1,subQ0]});Q154=makeQuery(id+"F0.imprint","IMPRINT",FACE,{"disambiguationData":[TD([[makeQuery(id+"F0.imprint","IMPRINT",EDGE,{"disambiguationData":[TD([[subQ2,-1.0]])],"derivedFrom":subQ1}),-1.0]])]});}
            var Q155;
            {var subQ0=sQuery(id+"F0.wireOp",EDGE,"E4.23.0");var subQ1=sQuery(id+"F0.wireOp",EDGE,"E0");var subQ2=makeQuery(id+"F0.imprint","INTERSECT",VERTEX,{"disambiguationData":[OD(1.0)],"derivedFrom":[subQ1,subQ0]});Q155=makeQuery(id+"F0.imprint","IMPRINT",FACE,{"disambiguationData":[TD([[makeQuery(id+"F0.imprint","IMPRINT",EDGE,{"disambiguationData":[TD([[subQ2,1.0]])],"derivedFrom":subQ1}),-1.0]])]});}
            var Q156;
            {var subQ0=sQuery(id+"F0.wireOp",EDGE,"E4.31.0");var subQ1=sQuery(id+"F0.wireOp",EDGE,"E0");var subQ2=makeQuery(id+"F0.imprint","INTERSECT",VERTEX,{"disambiguationData":[OD(1.0)],"derivedFrom":[subQ1,subQ0]});Q156=makeQuery(id+"F0.imprint","IMPRINT",FACE,{"disambiguationData":[TD([[makeQuery(id+"F0.imprint","IMPRINT",EDGE,{"disambiguationData":[TD([[subQ2,1.0]])],"derivedFrom":subQ1}),-1.0]])]});}
            var Q157;
            {var subQ0=sQuery(id+"F0.wireOp",EDGE,"E4.1.0");var subQ1=sQuery(id+"F0.wireOp",EDGE,"E0");var subQ2=makeQuery(id+"F0.imprint","INTERSECT",VERTEX,{"disambiguationData":[OD(1.0)],"derivedFrom":[subQ1,subQ0]});Q157=makeQuery(id+"F0.imprint","IMPRINT",FACE,{"disambiguationData":[TD([[makeQuery(id+"F0.imprint","IMPRINT",EDGE,{"disambiguationData":[TD([[subQ2,1.0]])],"derivedFrom":subQ1}),-1.0]])]});}
            var Q158;
            {var subQ0=sQuery(id+"F0.wireOp",EDGE,"E4.33.2");var subQ1=sQuery(id+"F0.wireOp",EDGE,"E0");var subQ2=makeQuery(id+"F0.imprint","INTERSECT",VERTEX,{"derivedFrom":[subQ1,subQ0]});Q158=makeQuery(id+"F0.imprint","IMPRINT",FACE,{"disambiguationData":[TD([[makeQuery(id+"F0.imprint","IMPRINT",EDGE,{"disambiguationData":[TD([[subQ2,-1.0]])],"derivedFrom":subQ1}),-1.0]])]});}
            var Q159;
            {var subQ0=sQuery(id+"F0.wireOp",EDGE,"E4.20.2");var subQ1=sQuery(id+"F0.wireOp",EDGE,"E0");var subQ2=makeQuery(id+"F0.imprint","INTERSECT",VERTEX,{"derivedFrom":[subQ1,subQ0]});Q159=makeQuery(id+"F0.imprint","IMPRINT",FACE,{"disambiguationData":[TD([[makeQuery(id+"F0.imprint","IMPRINT",EDGE,{"disambiguationData":[TD([[subQ2,-1.0]])],"derivedFrom":subQ1}),-1.0]])]});}
            var Q160;
            {var subQ0=sQuery(id+"F0.wireOp",EDGE,"E4.5.0");var subQ1=sQuery(id+"F0.wireOp",EDGE,"E0");var subQ2=makeQuery(id+"F0.imprint","INTERSECT",VERTEX,{"disambiguationData":[OD(1.0)],"derivedFrom":[subQ1,subQ0]});Q160=makeQuery(id+"F0.imprint","IMPRINT",FACE,{"disambiguationData":[TD([[makeQuery(id+"F0.imprint","IMPRINT",EDGE,{"disambiguationData":[TD([[subQ2,1.0]])],"derivedFrom":subQ1}),-1.0]])]});}
            var Q161;
            {var subQ0=sQuery(id+"F0.wireOp",EDGE,"E4.37.2");var subQ1=sQuery(id+"F0.wireOp",EDGE,"E0");var subQ2=makeQuery(id+"F0.imprint","INTERSECT",VERTEX,{"derivedFrom":[subQ1,subQ0]});Q161=makeQuery(id+"F0.imprint","IMPRINT",FACE,{"disambiguationData":[TD([[makeQuery(id+"F0.imprint","IMPRINT",EDGE,{"disambiguationData":[TD([[subQ2,-1.0]])],"derivedFrom":subQ1}),-1.0]])]});}
            var Q162;
            {var subQ0=sQuery(id+"F0.wireOp",EDGE,"E4.30.2");var subQ1=sQuery(id+"F0.wireOp",EDGE,"E0");var subQ2=makeQuery(id+"F0.imprint","INTERSECT",VERTEX,{"derivedFrom":[subQ1,subQ0]});Q162=makeQuery(id+"F0.imprint","IMPRINT",FACE,{"disambiguationData":[TD([[makeQuery(id+"F0.imprint","IMPRINT",EDGE,{"disambiguationData":[TD([[subQ2,-1.0]])],"derivedFrom":subQ1}),-1.0]])]});}
            var Q163;
            {var subQ0=sQuery(id+"F0.wireOp",EDGE,"E4.31.2");var subQ1=sQuery(id+"F0.wireOp",EDGE,"E0");var subQ2=makeQuery(id+"F0.imprint","INTERSECT",VERTEX,{"derivedFrom":[subQ1,subQ0]});Q163=makeQuery(id+"F0.imprint","IMPRINT",FACE,{"disambiguationData":[TD([[makeQuery(id+"F0.imprint","IMPRINT",EDGE,{"disambiguationData":[TD([[subQ2,-1.0]])],"derivedFrom":subQ1}),-1.0]])]});}
            var Q164;
            {var subQ0=sQuery(id+"F0.wireOp",EDGE,"E4.7.0");var subQ1=sQuery(id+"F0.wireOp",EDGE,"E0");var subQ2=makeQuery(id+"F0.imprint","INTERSECT",VERTEX,{"disambiguationData":[OD(0.0)],"derivedFrom":[subQ1,subQ0]});Q164=makeQuery(id+"F0.imprint","IMPRINT",FACE,{"disambiguationData":[TD([[makeQuery(id+"F0.imprint","IMPRINT",EDGE,{"disambiguationData":[TD([[subQ2,1.0]])],"derivedFrom":subQ1}),1.0]])]});}
            var Q165;
            {var subQ0=sQuery(id+"F0.wireOp",EDGE,"E4.8.0");var subQ1=sQuery(id+"F0.wireOp",EDGE,"E0");var subQ2=makeQuery(id+"F0.imprint","INTERSECT",VERTEX,{"disambiguationData":[OD(0.0)],"derivedFrom":[subQ1,subQ0]});Q165=makeQuery(id+"F0.imprint","IMPRINT",FACE,{"disambiguationData":[TD([[makeQuery(id+"F0.imprint","IMPRINT",EDGE,{"disambiguationData":[TD([[subQ2,1.0]])],"derivedFrom":subQ1}),1.0]])]});}
            var Q166;
            {var subQ0=sQuery(id+"F0.wireOp",EDGE,"E4.34.2");var subQ1=sQuery(id+"F0.wireOp",EDGE,"E0");var subQ2=makeQuery(id+"F0.imprint","INTERSECT",VERTEX,{"derivedFrom":[subQ1,subQ0]});Q166=makeQuery(id+"F0.imprint","IMPRINT",FACE,{"disambiguationData":[TD([[makeQuery(id+"F0.imprint","IMPRINT",EDGE,{"disambiguationData":[TD([[subQ2,-1.0]])],"derivedFrom":subQ1}),-1.0]])]});}
            var Q167;
            {var subQ0=sQuery(id+"F0.wireOp",EDGE,"E4.38.0");var subQ1=sQuery(id+"F0.wireOp",EDGE,"E0");var subQ2=makeQuery(id+"F0.imprint","INTERSECT",VERTEX,{"disambiguationData":[OD(0.0)],"derivedFrom":[subQ1,subQ0]});Q167=makeQuery(id+"F0.imprint","IMPRINT",FACE,{"disambiguationData":[TD([[makeQuery(id+"F0.imprint","IMPRINT",EDGE,{"disambiguationData":[TD([[subQ2,1.0]])],"derivedFrom":subQ1}),1.0]])]});}
            var Q168;
            {var subQ0=sQuery(id+"F0.wireOp",EDGE,"E4.25.0");var subQ1=sQuery(id+"F0.wireOp",EDGE,"E0");var subQ2=makeQuery(id+"F0.imprint","INTERSECT",VERTEX,{"disambiguationData":[OD(1.0)],"derivedFrom":[subQ1,subQ0]});Q168=makeQuery(id+"F0.imprint","IMPRINT",FACE,{"disambiguationData":[TD([[makeQuery(id+"F0.imprint","IMPRINT",EDGE,{"disambiguationData":[TD([[subQ2,1.0]])],"derivedFrom":subQ1}),-1.0]])]});}
            var Q169;
            {var subQ0=sQuery(id+"F0.wireOp",EDGE,"E4.18.0");var subQ1=sQuery(id+"F0.wireOp",EDGE,"E0");var subQ2=makeQuery(id+"F0.imprint","INTERSECT",VERTEX,{"disambiguationData":[OD(0.0)],"derivedFrom":[subQ1,subQ0]});Q169=makeQuery(id+"F0.imprint","IMPRINT",FACE,{"disambiguationData":[TD([[makeQuery(id+"F0.imprint","IMPRINT",EDGE,{"disambiguationData":[TD([[subQ2,1.0]])],"derivedFrom":subQ1}),1.0]])]});}
            var Q170;
            {var subQ0=sQuery(id+"F0.wireOp",EDGE,"E4.28.0");var subQ1=sQuery(id+"F0.wireOp",EDGE,"E0");var subQ2=makeQuery(id+"F0.imprint","INTERSECT",VERTEX,{"disambiguationData":[OD(0.0)],"derivedFrom":[subQ1,subQ0]});Q170=makeQuery(id+"F0.imprint","IMPRINT",FACE,{"disambiguationData":[TD([[makeQuery(id+"F0.imprint","IMPRINT",EDGE,{"disambiguationData":[TD([[subQ2,1.0]])],"derivedFrom":subQ1}),1.0]])]});}
            var Q171;
            {var subQ0=sQuery(id+"F0.wireOp",EDGE,"E4.36.2");var subQ1=sQuery(id+"F0.wireOp",EDGE,"E0");var subQ2=makeQuery(id+"F0.imprint","INTERSECT",VERTEX,{"derivedFrom":[subQ1,subQ0]});Q171=makeQuery(id+"F0.imprint","IMPRINT",FACE,{"disambiguationData":[TD([[makeQuery(id+"F0.imprint","IMPRINT",EDGE,{"disambiguationData":[TD([[subQ2,-1.0]])],"derivedFrom":subQ1}),-1.0]])]});}
            var Q172;
            {var subQ0=sQuery(id+"F0.wireOp",EDGE,"E4.35.0");var subQ1=sQuery(id+"F0.wireOp",EDGE,"E0");var subQ2=makeQuery(id+"F0.imprint","INTERSECT",VERTEX,{"disambiguationData":[OD(1.0)],"derivedFrom":[subQ1,subQ0]});Q172=makeQuery(id+"F0.imprint","IMPRINT",FACE,{"disambiguationData":[TD([[makeQuery(id+"F0.imprint","IMPRINT",EDGE,{"disambiguationData":[TD([[subQ2,1.0]])],"derivedFrom":subQ1}),-1.0]])]});}
            var Q173;
            {var subQ0=sQuery(id+"F0.wireOp",EDGE,"E4.13.0");var subQ1=sQuery(id+"F0.wireOp",EDGE,"E0");var subQ2=makeQuery(id+"F0.imprint","INTERSECT",VERTEX,{"disambiguationData":[OD(0.0)],"derivedFrom":[subQ1,subQ0]});Q173=makeQuery(id+"F0.imprint","IMPRINT",FACE,{"disambiguationData":[TD([[makeQuery(id+"F0.imprint","IMPRINT",EDGE,{"disambiguationData":[TD([[subQ2,1.0]])],"derivedFrom":subQ1}),1.0]])]});}
            var Q174;
            {var subQ0=sQuery(id+"F0.wireOp",EDGE,"E4.20.0");var subQ1=sQuery(id+"F0.wireOp",EDGE,"E0");var subQ2=makeQuery(id+"F0.imprint","INTERSECT",VERTEX,{"disambiguationData":[OD(1.0)],"derivedFrom":[subQ1,subQ0]});Q174=makeQuery(id+"F0.imprint","IMPRINT",FACE,{"disambiguationData":[TD([[makeQuery(id+"F0.imprint","IMPRINT",EDGE,{"disambiguationData":[TD([[subQ2,1.0]])],"derivedFrom":subQ1}),-1.0]])]});}
            var Q175;
            {var subQ0=sQuery(id+"F0.wireOp",EDGE,"E4.29.0");var subQ1=sQuery(id+"F0.wireOp",EDGE,"E0");var subQ2=makeQuery(id+"F0.imprint","INTERSECT",VERTEX,{"disambiguationData":[OD(0.0)],"derivedFrom":[subQ1,subQ0]});Q175=makeQuery(id+"F0.imprint","IMPRINT",FACE,{"disambiguationData":[TD([[makeQuery(id+"F0.imprint","IMPRINT",EDGE,{"disambiguationData":[TD([[subQ2,1.0]])],"derivedFrom":subQ1}),1.0]])]});}
            var Q176;
            {var subQ0=sQuery(id+"F0.wireOp",EDGE,"E4.1.0");var subQ1=sQuery(id+"F0.wireOp",EDGE,"E0");var subQ2=makeQuery(id+"F0.imprint","INTERSECT",VERTEX,{"disambiguationData":[OD(0.0)],"derivedFrom":[subQ1,subQ0]});Q176=makeQuery(id+"F0.imprint","IMPRINT",FACE,{"disambiguationData":[TD([[makeQuery(id+"F0.imprint","IMPRINT",EDGE,{"disambiguationData":[TD([[subQ2,1.0]])],"derivedFrom":subQ1}),1.0]])]});}
            var Q177;
            {var subQ0=sQuery(id+"F0.wireOp",EDGE,"E4.17.0");var subQ1=sQuery(id+"F0.wireOp",EDGE,"E0");var subQ2=makeQuery(id+"F0.imprint","INTERSECT",VERTEX,{"disambiguationData":[OD(0.0)],"derivedFrom":[subQ1,subQ0]});Q177=makeQuery(id+"F0.imprint","IMPRINT",FACE,{"disambiguationData":[TD([[makeQuery(id+"F0.imprint","IMPRINT",EDGE,{"disambiguationData":[TD([[subQ2,1.0]])],"derivedFrom":subQ1}),1.0]])]});}
            var Q178;
            {var subQ0=sQuery(id+"F0.wireOp",EDGE,"E4.11.2");var subQ1=sQuery(id+"F0.wireOp",EDGE,"E0");var subQ2=makeQuery(id+"F0.imprint","INTERSECT",VERTEX,{"derivedFrom":[subQ1,subQ0]});Q178=makeQuery(id+"F0.imprint","IMPRINT",FACE,{"disambiguationData":[TD([[makeQuery(id+"F0.imprint","IMPRINT",EDGE,{"disambiguationData":[TD([[subQ2,-1.0]])],"derivedFrom":subQ1}),-1.0]])]});}
            var Q179;
            {var subQ0=sQuery(id+"F0.wireOp",EDGE,"E4.14.0");var subQ1=sQuery(id+"F0.wireOp",EDGE,"E0");var subQ2=makeQuery(id+"F0.imprint","INTERSECT",VERTEX,{"disambiguationData":[OD(0.0)],"derivedFrom":[subQ1,subQ0]});Q179=makeQuery(id+"F0.imprint","IMPRINT",FACE,{"disambiguationData":[TD([[makeQuery(id+"F0.imprint","IMPRINT",EDGE,{"disambiguationData":[TD([[subQ2,1.0]])],"derivedFrom":subQ1}),1.0]])]});}
            var Q180;
            {var subQ0=sQuery(id+"F0.wireOp",EDGE,"E4.12.0");var subQ1=sQuery(id+"F0.wireOp",EDGE,"E0");var subQ2=makeQuery(id+"F0.imprint","INTERSECT",VERTEX,{"disambiguationData":[OD(0.0)],"derivedFrom":[subQ1,subQ0]});Q180=makeQuery(id+"F0.imprint","IMPRINT",FACE,{"disambiguationData":[TD([[makeQuery(id+"F0.imprint","IMPRINT",EDGE,{"disambiguationData":[TD([[subQ2,1.0]])],"derivedFrom":subQ1}),1.0]])]});}
            var Q181;
            {var subQ0=sQuery(id+"F0.wireOp",EDGE,"E4.7.2");var subQ1=sQuery(id+"F0.wireOp",EDGE,"E0");var subQ2=makeQuery(id+"F0.imprint","INTERSECT",VERTEX,{"derivedFrom":[subQ1,subQ0]});Q181=makeQuery(id+"F0.imprint","IMPRINT",FACE,{"disambiguationData":[TD([[makeQuery(id+"F0.imprint","IMPRINT",EDGE,{"disambiguationData":[TD([[subQ2,-1.0]])],"derivedFrom":subQ1}),-1.0]])]});}
            var Q182;
            {var subQ0=sQuery(id+"F0.wireOp",EDGE,"E4.16.2");var subQ1=sQuery(id+"F0.wireOp",EDGE,"E0");var subQ2=makeQuery(id+"F0.imprint","INTERSECT",VERTEX,{"derivedFrom":[subQ1,subQ0]});Q182=makeQuery(id+"F0.imprint","IMPRINT",FACE,{"disambiguationData":[TD([[makeQuery(id+"F0.imprint","IMPRINT",EDGE,{"disambiguationData":[TD([[subQ2,-1.0]])],"derivedFrom":subQ1}),-1.0]])]});}
            var Q183;
            {var subQ0=sQuery(id+"F0.wireOp",EDGE,"E4.26.0");var subQ1=sQuery(id+"F0.wireOp",EDGE,"E0");var subQ2=makeQuery(id+"F0.imprint","INTERSECT",VERTEX,{"disambiguationData":[OD(1.0)],"derivedFrom":[subQ1,subQ0]});Q183=makeQuery(id+"F0.imprint","IMPRINT",FACE,{"disambiguationData":[TD([[makeQuery(id+"F0.imprint","IMPRINT",EDGE,{"disambiguationData":[TD([[subQ2,1.0]])],"derivedFrom":subQ1}),-1.0]])]});}
            var Q184;
            {var subQ0=sQuery(id+"F0.wireOp",EDGE,"E4.34.0");var subQ1=sQuery(id+"F0.wireOp",EDGE,"E0");var subQ2=makeQuery(id+"F0.imprint","INTERSECT",VERTEX,{"disambiguationData":[OD(1.0)],"derivedFrom":[subQ1,subQ0]});Q184=makeQuery(id+"F0.imprint","IMPRINT",FACE,{"disambiguationData":[TD([[makeQuery(id+"F0.imprint","IMPRINT",EDGE,{"disambiguationData":[TD([[subQ2,1.0]])],"derivedFrom":subQ1}),-1.0]])]});}
            var Q185;
            {var subQ0=sQuery(id+"F0.wireOp",EDGE,"E4.30.0");var subQ1=sQuery(id+"F0.wireOp",EDGE,"E0");var subQ2=makeQuery(id+"F0.imprint","INTERSECT",VERTEX,{"disambiguationData":[OD(1.0)],"derivedFrom":[subQ1,subQ0]});Q185=makeQuery(id+"F0.imprint","IMPRINT",FACE,{"disambiguationData":[TD([[makeQuery(id+"F0.imprint","IMPRINT",EDGE,{"disambiguationData":[TD([[subQ2,1.0]])],"derivedFrom":subQ1}),-1.0]])]});}
            var Q186;
            {var subQ0=sQuery(id+"F0.wireOp",EDGE,"E4.22.0");var subQ1=sQuery(id+"F0.wireOp",EDGE,"E0");var subQ2=makeQuery(id+"F0.imprint","INTERSECT",VERTEX,{"disambiguationData":[OD(0.0)],"derivedFrom":[subQ1,subQ0]});Q186=makeQuery(id+"F0.imprint","IMPRINT",FACE,{"disambiguationData":[TD([[makeQuery(id+"F0.imprint","IMPRINT",EDGE,{"disambiguationData":[TD([[subQ2,1.0]])],"derivedFrom":subQ1}),1.0]])]});}
            var Q187;
            {var subQ0=sQuery(id+"F0.wireOp",EDGE,"E4.32.0");var subQ1=sQuery(id+"F0.wireOp",EDGE,"E0");var subQ2=makeQuery(id+"F0.imprint","INTERSECT",VERTEX,{"disambiguationData":[OD(0.0)],"derivedFrom":[subQ1,subQ0]});Q187=makeQuery(id+"F0.imprint","IMPRINT",FACE,{"disambiguationData":[TD([[makeQuery(id+"F0.imprint","IMPRINT",EDGE,{"disambiguationData":[TD([[subQ2,1.0]])],"derivedFrom":subQ1}),1.0]])]});}
            var Q188;
            {var subQ0=sQuery(id+"F0.wireOp",EDGE,"E4.38.0");var subQ1=sQuery(id+"F0.wireOp",EDGE,"E0");var subQ2=makeQuery(id+"F0.imprint","INTERSECT",VERTEX,{"disambiguationData":[OD(1.0)],"derivedFrom":[subQ1,subQ0]});Q188=makeQuery(id+"F0.imprint","IMPRINT",FACE,{"disambiguationData":[TD([[makeQuery(id+"F0.imprint","IMPRINT",EDGE,{"disambiguationData":[TD([[subQ2,1.0]])],"derivedFrom":subQ1}),-1.0]])]});}
            var Q189;
            {var subQ0=sQuery(id+"F0.wireOp",EDGE,"E4.29.2");var subQ1=sQuery(id+"F0.wireOp",EDGE,"E0");var subQ2=makeQuery(id+"F0.imprint","INTERSECT",VERTEX,{"derivedFrom":[subQ1,subQ0]});Q189=makeQuery(id+"F0.imprint","IMPRINT",FACE,{"disambiguationData":[TD([[makeQuery(id+"F0.imprint","IMPRINT",EDGE,{"disambiguationData":[TD([[subQ2,-1.0]])],"derivedFrom":subQ1}),-1.0]])]});}
            var Q190;
            {var subQ0=sQuery(id+"F0.wireOp",EDGE,"E4.21.0");var subQ1=sQuery(id+"F0.wireOp",EDGE,"E0");var subQ2=makeQuery(id+"F0.imprint","INTERSECT",VERTEX,{"disambiguationData":[OD(0.0)],"derivedFrom":[subQ1,subQ0]});Q190=makeQuery(id+"F0.imprint","IMPRINT",FACE,{"disambiguationData":[TD([[makeQuery(id+"F0.imprint","IMPRINT",EDGE,{"disambiguationData":[TD([[subQ2,1.0]])],"derivedFrom":subQ1}),1.0]])]});}
            var Q191;
            {var subQ0=sQuery(id+"F0.wireOp",EDGE,"E4.11.0");var subQ1=sQuery(id+"F0.wireOp",EDGE,"E0");var subQ2=makeQuery(id+"F0.imprint","INTERSECT",VERTEX,{"disambiguationData":[OD(0.0)],"derivedFrom":[subQ1,subQ0]});Q191=makeQuery(id+"F0.imprint","IMPRINT",FACE,{"disambiguationData":[TD([[makeQuery(id+"F0.imprint","IMPRINT",EDGE,{"disambiguationData":[TD([[subQ2,1.0]])],"derivedFrom":subQ1}),1.0]])]});}
            var Q192;
            {var subQ0=sQuery(id+"F0.wireOp",EDGE,"E4.27.0");var subQ1=sQuery(id+"F0.wireOp",EDGE,"E0");var subQ2=makeQuery(id+"F0.imprint","INTERSECT",VERTEX,{"disambiguationData":[OD(0.0)],"derivedFrom":[subQ1,subQ0]});Q192=makeQuery(id+"F0.imprint","IMPRINT",FACE,{"disambiguationData":[TD([[makeQuery(id+"F0.imprint","IMPRINT",EDGE,{"disambiguationData":[TD([[subQ2,1.0]])],"derivedFrom":subQ1}),1.0]])]});}
            var Q193;
            {var subQ0=sQuery(id+"F0.wireOp",EDGE,"E4.19.2");var subQ1=sQuery(id+"F0.wireOp",EDGE,"E0");var subQ2=makeQuery(id+"F0.imprint","INTERSECT",VERTEX,{"derivedFrom":[subQ1,subQ0]});Q193=makeQuery(id+"F0.imprint","IMPRINT",FACE,{"disambiguationData":[TD([[makeQuery(id+"F0.imprint","IMPRINT",EDGE,{"disambiguationData":[TD([[subQ2,-1.0]])],"derivedFrom":subQ1}),-1.0]])]});}
            var Q194;
            {var subQ0=sQuery(id+"F0.wireOp",EDGE,"E4.25.0");var subQ1=sQuery(id+"F0.wireOp",EDGE,"E0");var subQ2=makeQuery(id+"F0.imprint","INTERSECT",VERTEX,{"disambiguationData":[OD(0.0)],"derivedFrom":[subQ1,subQ0]});Q194=makeQuery(id+"F0.imprint","IMPRINT",FACE,{"disambiguationData":[TD([[makeQuery(id+"F0.imprint","IMPRINT",EDGE,{"disambiguationData":[TD([[subQ2,1.0]])],"derivedFrom":subQ1}),1.0]])]});}
            var Q195;
            {var subQ0=sQuery(id+"F0.wireOp",EDGE,"E4.23.0");var subQ1=sQuery(id+"F0.wireOp",EDGE,"E0");var subQ2=makeQuery(id+"F0.imprint","INTERSECT",VERTEX,{"disambiguationData":[OD(0.0)],"derivedFrom":[subQ1,subQ0]});Q195=makeQuery(id+"F0.imprint","IMPRINT",FACE,{"disambiguationData":[TD([[makeQuery(id+"F0.imprint","IMPRINT",EDGE,{"disambiguationData":[TD([[subQ2,1.0]])],"derivedFrom":subQ1}),1.0]])]});}
            var Q196;
            {var subQ0=sQuery(id+"F0.wireOp",EDGE,"E4.39.2");var subQ1=sQuery(id+"F0.wireOp",EDGE,"E0");var subQ2=makeQuery(id+"F0.imprint","INTERSECT",VERTEX,{"derivedFrom":[subQ1,subQ0]});Q196=makeQuery(id+"F0.imprint","IMPRINT",FACE,{"disambiguationData":[TD([[makeQuery(id+"F0.imprint","IMPRINT",EDGE,{"disambiguationData":[TD([[subQ2,-1.0]])],"derivedFrom":subQ1}),-1.0]])]});}
            var Q197;
            {var subQ0=sQuery(id+"F0.wireOp",EDGE,"E4.28.2");var subQ1=sQuery(id+"F0.wireOp",EDGE,"E0");var subQ2=makeQuery(id+"F0.imprint","INTERSECT",VERTEX,{"derivedFrom":[subQ1,subQ0]});Q197=makeQuery(id+"F0.imprint","IMPRINT",FACE,{"disambiguationData":[TD([[makeQuery(id+"F0.imprint","IMPRINT",EDGE,{"disambiguationData":[TD([[subQ2,-1.0]])],"derivedFrom":subQ1}),-1.0]])]});}
            var Q198;
            {var subQ0=sQuery(id+"F0.wireOp",EDGE,"E4.11.0");var subQ1=sQuery(id+"F0.wireOp",EDGE,"E0");var subQ2=makeQuery(id+"F0.imprint","INTERSECT",VERTEX,{"disambiguationData":[OD(1.0)],"derivedFrom":[subQ1,subQ0]});Q198=makeQuery(id+"F0.imprint","IMPRINT",FACE,{"disambiguationData":[TD([[makeQuery(id+"F0.imprint","IMPRINT",EDGE,{"disambiguationData":[TD([[subQ2,1.0]])],"derivedFrom":subQ1}),-1.0]])]});}
            var Q199;
            {var subQ0=sQuery(id+"F0.wireOp",EDGE,"E4.2.0");var subQ1=sQuery(id+"F0.wireOp",EDGE,"E0");var subQ2=makeQuery(id+"F0.imprint","INTERSECT",VERTEX,{"disambiguationData":[OD(0.0)],"derivedFrom":[subQ1,subQ0]});Q199=makeQuery(id+"F0.imprint","IMPRINT",FACE,{"disambiguationData":[TD([[makeQuery(id+"F0.imprint","IMPRINT",EDGE,{"disambiguationData":[TD([[subQ2,1.0]])],"derivedFrom":subQ1}),1.0]])]});}
            var Q200;
            {var subQ0=sQuery(id+"F0.wireOp",EDGE,"E4.17.2");var subQ1=sQuery(id+"F0.wireOp",EDGE,"E0");var subQ2=makeQuery(id+"F0.imprint","INTERSECT",VERTEX,{"derivedFrom":[subQ1,subQ0]});Q200=makeQuery(id+"F0.imprint","IMPRINT",FACE,{"disambiguationData":[TD([[makeQuery(id+"F0.imprint","IMPRINT",EDGE,{"disambiguationData":[TD([[subQ2,-1.0]])],"derivedFrom":subQ1}),-1.0]])]});}
            extrude(context, id + "F1", {"entities" : qUnion([Q0, Q1, Q2, Q3, Q4, Q5, Q6, Q7, Q8, Q9, Q10, Q11, Q12, Q13, Q14, Q15, Q16, Q17, Q18, Q19, Q20, Q21, Q22, Q23, Q24, Q25, Q26, Q27, Q28, Q29, Q30, Q31, Q32, Q33, Q34, Q35, Q36, Q37, Q38, Q39, Q40, Q41, Q42, Q43, Q44, Q45, Q46, Q47, Q48, Q49, Q50, Q51, Q52, Q53, Q54, Q55, Q56, Q57, Q58, Q59, Q60, Q61, Q62, Q63, Q64, Q65, Q66, Q67, Q68, Q69, Q70, Q71, Q72, Q73, Q74, Q75, Q76, Q77, Q78, Q79, Q80, Q81, Q82, Q83, Q84, Q85, Q86, Q87, Q88, Q89, Q90, Q91, Q92, Q93, Q94, Q95, Q96, Q97, Q98, Q99, Q100, Q101, Q102, Q103, Q104, Q105, Q106, Q107, Q108, Q109, Q110, Q111, Q112, Q113, Q114, Q115, Q116, Q117, Q118, Q119, Q120, Q121, Q122, Q123, Q124, Q125, Q126, Q127, Q128, Q129, Q130, Q131, Q132, Q133, Q134, Q135, Q136, Q137, Q138, Q139, Q140, Q141, Q142, Q143, Q144, Q145, Q146, Q147, Q148, Q149, Q150, Q151, Q152, Q153, Q154, Q155, Q156, Q157, Q158, Q159, Q160, Q161, Q162, Q163, Q164, Q165, Q166, Q167, Q168, Q169, Q170, Q171, Q172, Q173, Q174, Q175, Q176, Q177, Q178, Q179, Q180, Q181, Q182, Q183, Q184, Q185, Q186, Q187, Q188, Q189, Q190, Q191, Q192, Q193, Q194, Q195, Q196, Q197, Q198, Q199, Q200]), "depth" : 11 * mm, "offsetDistance" : 25 * mm});
        }
        {
            var Q0;
            Q0=makeQuery(id+"F1.opExtrude","CAP_FACE",FACE,{"disambiguationData":[OSD([sQuery(id+"F0.wireOp",EDGE,"E0"),sQuery(id+"F0.wireOp",EDGE,"E1"),sQuery(id+"F0.wireOp",EDGE,"E2"),sQuery(id+"F0.wireOp",EDGE,"E3"),sQuery(id+"F0.wireOp",EDGE,"E4.1.0"),sQuery(id+"F0.wireOp",EDGE,"E4.1.1"),sQuery(id+"F0.wireOp",EDGE,"E4.1.2"),sQuery(id+"F0.wireOp",EDGE,"E4.2.0"),sQuery(id+"F0.wireOp",EDGE,"E4.2.1"),sQuery(id+"F0.wireOp",EDGE,"E4.2.2"),sQuery(id+"F0.wireOp",EDGE,"E4.3.0"),sQuery(id+"F0.wireOp",EDGE,"E4.3.1"),sQuery(id+"F0.wireOp",EDGE,"E4.3.2"),sQuery(id+"F0.wireOp",EDGE,"E4.4.0"),sQuery(id+"F0.wireOp",EDGE,"E4.4.1"),sQuery(id+"F0.wireOp",EDGE,"E4.4.2"),sQuery(id+"F0.wireOp",EDGE,"E4.5.0"),sQuery(id+"F0.wireOp",EDGE,"E4.5.1"),sQuery(id+"F0.wireOp",EDGE,"E4.5.2"),sQuery(id+"F0.wireOp",EDGE,"E4.6.0"),sQuery(id+"F0.wireOp",EDGE,"E4.6.1"),sQuery(id+"F0.wireOp",EDGE,"E4.6.2"),sQuery(id+"F0.wireOp",EDGE,"E4.7.0"),sQuery(id+"F0.wireOp",EDGE,"E4.7.1"),sQuery(id+"F0.wireOp",EDGE,"E4.7.2"),sQuery(id+"F0.wireOp",EDGE,"E4.8.0"),sQuery(id+"F0.wireOp",EDGE,"E4.8.1"),sQuery(id+"F0.wireOp",EDGE,"E4.8.2"),sQuery(id+"F0.wireOp",EDGE,"E4.9.0"),sQuery(id+"F0.wireOp",EDGE,"E4.9.1"),sQuery(id+"F0.wireOp",EDGE,"E4.9.2"),sQuery(id+"F0.wireOp",EDGE,"E4.10.0"),sQuery(id+"F0.wireOp",EDGE,"E4.10.1"),sQuery(id+"F0.wireOp",EDGE,"E4.10.2"),sQuery(id+"F0.wireOp",EDGE,"E4.11.0"),sQuery(id+"F0.wireOp",EDGE,"E4.11.1"),sQuery(id+"F0.wireOp",EDGE,"E4.11.2"),sQuery(id+"F0.wireOp",EDGE,"E4.12.0"),sQuery(id+"F0.wireOp",EDGE,"E4.12.1"),sQuery(id+"F0.wireOp",EDGE,"E4.12.2"),sQuery(id+"F0.wireOp",EDGE,"E4.13.0"),sQuery(id+"F0.wireOp",EDGE,"E4.13.1"),sQuery(id+"F0.wireOp",EDGE,"E4.13.2"),sQuery(id+"F0.wireOp",EDGE,"E4.14.0"),sQuery(id+"F0.wireOp",EDGE,"E4.14.1"),sQuery(id+"F0.wireOp",EDGE,"E4.14.2"),sQuery(id+"F0.wireOp",EDGE,"E4.15.0"),sQuery(id+"F0.wireOp",EDGE,"E4.15.1"),sQuery(id+"F0.wireOp",EDGE,"E4.15.2"),sQuery(id+"F0.wireOp",EDGE,"E4.16.0"),sQuery(id+"F0.wireOp",EDGE,"E4.16.1"),sQuery(id+"F0.wireOp",EDGE,"E4.16.2"),sQuery(id+"F0.wireOp",EDGE,"E4.17.0"),sQuery(id+"F0.wireOp",EDGE,"E4.17.1"),sQuery(id+"F0.wireOp",EDGE,"E4.17.2"),sQuery(id+"F0.wireOp",EDGE,"E4.18.0"),sQuery(id+"F0.wireOp",EDGE,"E4.18.1"),sQuery(id+"F0.wireOp",EDGE,"E4.18.2"),sQuery(id+"F0.wireOp",EDGE,"E4.19.0"),sQuery(id+"F0.wireOp",EDGE,"E4.19.1"),sQuery(id+"F0.wireOp",EDGE,"E4.19.2"),sQuery(id+"F0.wireOp",EDGE,"E4.20.0"),sQuery(id+"F0.wireOp",EDGE,"E4.20.1"),sQuery(id+"F0.wireOp",EDGE,"E4.20.2"),sQuery(id+"F0.wireOp",EDGE,"E4.21.0"),sQuery(id+"F0.wireOp",EDGE,"E4.21.1"),sQuery(id+"F0.wireOp",EDGE,"E4.21.2"),sQuery(id+"F0.wireOp",EDGE,"E4.22.0"),sQuery(id+"F0.wireOp",EDGE,"E4.22.1"),sQuery(id+"F0.wireOp",EDGE,"E4.22.2"),sQuery(id+"F0.wireOp",EDGE,"E4.23.0"),sQuery(id+"F0.wireOp",EDGE,"E4.23.1"),sQuery(id+"F0.wireOp",EDGE,"E4.23.2"),sQuery(id+"F0.wireOp",EDGE,"E4.24.0"),sQuery(id+"F0.wireOp",EDGE,"E4.24.1"),sQuery(id+"F0.wireOp",EDGE,"E4.24.2"),sQuery(id+"F0.wireOp",EDGE,"E4.25.0"),sQuery(id+"F0.wireOp",EDGE,"E4.25.1"),sQuery(id+"F0.wireOp",EDGE,"E4.25.2"),sQuery(id+"F0.wireOp",EDGE,"E4.26.0"),sQuery(id+"F0.wireOp",EDGE,"E4.26.1"),sQuery(id+"F0.wireOp",EDGE,"E4.26.2"),sQuery(id+"F0.wireOp",EDGE,"E4.27.0"),sQuery(id+"F0.wireOp",EDGE,"E4.27.1"),sQuery(id+"F0.wireOp",EDGE,"E4.27.2"),sQuery(id+"F0.wireOp",EDGE,"E4.28.0"),sQuery(id+"F0.wireOp",EDGE,"E4.28.1"),sQuery(id+"F0.wireOp",EDGE,"E4.28.2"),sQuery(id+"F0.wireOp",EDGE,"E4.29.0"),sQuery(id+"F0.wireOp",EDGE,"E4.29.1"),sQuery(id+"F0.wireOp",EDGE,"E4.29.2"),sQuery(id+"F0.wireOp",EDGE,"E4.30.0"),sQuery(id+"F0.wireOp",EDGE,"E4.30.1"),sQuery(id+"F0.wireOp",EDGE,"E4.30.2"),sQuery(id+"F0.wireOp",EDGE,"E4.31.0"),sQuery(id+"F0.wireOp",EDGE,"E4.31.1"),sQuery(id+"F0.wireOp",EDGE,"E4.31.2"),sQuery(id+"F0.wireOp",EDGE,"E4.32.0"),sQuery(id+"F0.wireOp",EDGE,"E4.32.1"),sQuery(id+"F0.wireOp",EDGE,"E4.32.2"),sQuery(id+"F0.wireOp",EDGE,"E4.33.0"),sQuery(id+"F0.wireOp",EDGE,"E4.33.1"),sQuery(id+"F0.wireOp",EDGE,"E4.33.2"),sQuery(id+"F0.wireOp",EDGE,"E4.34.0"),sQuery(id+"F0.wireOp",EDGE,"E4.34.1"),sQuery(id+"F0.wireOp",EDGE,"E4.34.2"),sQuery(id+"F0.wireOp",EDGE,"E4.35.0"),sQuery(id+"F0.wireOp",EDGE,"E4.35.1"),sQuery(id+"F0.wireOp",EDGE,"E4.35.2"),sQuery(id+"F0.wireOp",EDGE,"E4.36.0"),sQuery(id+"F0.wireOp",EDGE,"E4.36.1"),sQuery(id+"F0.wireOp",EDGE,"E4.36.2"),sQuery(id+"F0.wireOp",EDGE,"E4.37.0"),sQuery(id+"F0.wireOp",EDGE,"E4.37.1"),sQuery(id+"F0.wireOp",EDGE,"E4.37.2"),sQuery(id+"F0.wireOp",EDGE,"E4.38.0"),sQuery(id+"F0.wireOp",EDGE,"E4.38.1"),sQuery(id+"F0.wireOp",EDGE,"E4.38.2"),sQuery(id+"F0.wireOp",EDGE,"E4.39.0"),sQuery(id+"F0.wireOp",EDGE,"E4.39.1"),sQuery(id+"F0.wireOp",EDGE,"E4.39.2")])],"isStart":true});
            var sketch = newSketch(context, id + "F2", { "sketchPlane" : qUnion([Q0])});
            skCircle(sketch, "E5", {"center": v(0, 0) * mm, "radius": 34 * mm});
            skSolve(sketch);
        }
        {
            var Q0;
            Q0=makeQuery(id+"F1.opExtrude","CAP_FACE",FACE,{"disambiguationData":[OSD([sQuery(id+"F0.wireOp",EDGE,"E0"),sQuery(id+"F0.wireOp",EDGE,"E1"),sQuery(id+"F0.wireOp",EDGE,"E2"),sQuery(id+"F0.wireOp",EDGE,"E3"),sQuery(id+"F0.wireOp",EDGE,"E4.1.0"),sQuery(id+"F0.wireOp",EDGE,"E4.1.1"),sQuery(id+"F0.wireOp",EDGE,"E4.1.2"),sQuery(id+"F0.wireOp",EDGE,"E4.2.0"),sQuery(id+"F0.wireOp",EDGE,"E4.2.1"),sQuery(id+"F0.wireOp",EDGE,"E4.2.2"),sQuery(id+"F0.wireOp",EDGE,"E4.3.0"),sQuery(id+"F0.wireOp",EDGE,"E4.3.1"),sQuery(id+"F0.wireOp",EDGE,"E4.3.2"),sQuery(id+"F0.wireOp",EDGE,"E4.4.0"),sQuery(id+"F0.wireOp",EDGE,"E4.4.1"),sQuery(id+"F0.wireOp",EDGE,"E4.4.2"),sQuery(id+"F0.wireOp",EDGE,"E4.5.0"),sQuery(id+"F0.wireOp",EDGE,"E4.5.1"),sQuery(id+"F0.wireOp",EDGE,"E4.5.2"),sQuery(id+"F0.wireOp",EDGE,"E4.6.0"),sQuery(id+"F0.wireOp",EDGE,"E4.6.1"),sQuery(id+"F0.wireOp",EDGE,"E4.6.2"),sQuery(id+"F0.wireOp",EDGE,"E4.7.0"),sQuery(id+"F0.wireOp",EDGE,"E4.7.1"),sQuery(id+"F0.wireOp",EDGE,"E4.7.2"),sQuery(id+"F0.wireOp",EDGE,"E4.8.0"),sQuery(id+"F0.wireOp",EDGE,"E4.8.1"),sQuery(id+"F0.wireOp",EDGE,"E4.8.2"),sQuery(id+"F0.wireOp",EDGE,"E4.9.0"),sQuery(id+"F0.wireOp",EDGE,"E4.9.1"),sQuery(id+"F0.wireOp",EDGE,"E4.9.2"),sQuery(id+"F0.wireOp",EDGE,"E4.10.0"),sQuery(id+"F0.wireOp",EDGE,"E4.10.1"),sQuery(id+"F0.wireOp",EDGE,"E4.10.2"),sQuery(id+"F0.wireOp",EDGE,"E4.11.0"),sQuery(id+"F0.wireOp",EDGE,"E4.11.1"),sQuery(id+"F0.wireOp",EDGE,"E4.11.2"),sQuery(id+"F0.wireOp",EDGE,"E4.12.0"),sQuery(id+"F0.wireOp",EDGE,"E4.12.1"),sQuery(id+"F0.wireOp",EDGE,"E4.12.2"),sQuery(id+"F0.wireOp",EDGE,"E4.13.0"),sQuery(id+"F0.wireOp",EDGE,"E4.13.1"),sQuery(id+"F0.wireOp",EDGE,"E4.13.2"),sQuery(id+"F0.wireOp",EDGE,"E4.14.0"),sQuery(id+"F0.wireOp",EDGE,"E4.14.1"),sQuery(id+"F0.wireOp",EDGE,"E4.14.2"),sQuery(id+"F0.wireOp",EDGE,"E4.15.0"),sQuery(id+"F0.wireOp",EDGE,"E4.15.1"),sQuery(id+"F0.wireOp",EDGE,"E4.15.2"),sQuery(id+"F0.wireOp",EDGE,"E4.16.0"),sQuery(id+"F0.wireOp",EDGE,"E4.16.1"),sQuery(id+"F0.wireOp",EDGE,"E4.16.2"),sQuery(id+"F0.wireOp",EDGE,"E4.17.0"),sQuery(id+"F0.wireOp",EDGE,"E4.17.1"),sQuery(id+"F0.wireOp",EDGE,"E4.17.2"),sQuery(id+"F0.wireOp",EDGE,"E4.18.0"),sQuery(id+"F0.wireOp",EDGE,"E4.18.1"),sQuery(id+"F0.wireOp",EDGE,"E4.18.2"),sQuery(id+"F0.wireOp",EDGE,"E4.19.0"),sQuery(id+"F0.wireOp",EDGE,"E4.19.1"),sQuery(id+"F0.wireOp",EDGE,"E4.19.2"),sQuery(id+"F0.wireOp",EDGE,"E4.20.0"),sQuery(id+"F0.wireOp",EDGE,"E4.20.1"),sQuery(id+"F0.wireOp",EDGE,"E4.20.2"),sQuery(id+"F0.wireOp",EDGE,"E4.21.0"),sQuery(id+"F0.wireOp",EDGE,"E4.21.1"),sQuery(id+"F0.wireOp",EDGE,"E4.21.2"),sQuery(id+"F0.wireOp",EDGE,"E4.22.0"),sQuery(id+"F0.wireOp",EDGE,"E4.22.1"),sQuery(id+"F0.wireOp",EDGE,"E4.22.2"),sQuery(id+"F0.wireOp",EDGE,"E4.23.0"),sQuery(id+"F0.wireOp",EDGE,"E4.23.1"),sQuery(id+"F0.wireOp",EDGE,"E4.23.2"),sQuery(id+"F0.wireOp",EDGE,"E4.24.0"),sQuery(id+"F0.wireOp",EDGE,"E4.24.1"),sQuery(id+"F0.wireOp",EDGE,"E4.24.2"),sQuery(id+"F0.wireOp",EDGE,"E4.25.0"),sQuery(id+"F0.wireOp",EDGE,"E4.25.1"),sQuery(id+"F0.wireOp",EDGE,"E4.25.2"),sQuery(id+"F0.wireOp",EDGE,"E4.26.0"),sQuery(id+"F0.wireOp",EDGE,"E4.26.1"),sQuery(id+"F0.wireOp",EDGE,"E4.26.2"),sQuery(id+"F0.wireOp",EDGE,"E4.27.0"),sQuery(id+"F0.wireOp",EDGE,"E4.27.1"),sQuery(id+"F0.wireOp",EDGE,"E4.27.2"),sQuery(id+"F0.wireOp",EDGE,"E4.28.0"),sQuery(id+"F0.wireOp",EDGE,"E4.28.1"),sQuery(id+"F0.wireOp",EDGE,"E4.28.2"),sQuery(id+"F0.wireOp",EDGE,"E4.29.0"),sQuery(id+"F0.wireOp",EDGE,"E4.29.1"),sQuery(id+"F0.wireOp",EDGE,"E4.29.2"),sQuery(id+"F0.wireOp",EDGE,"E4.30.0"),sQuery(id+"F0.wireOp",EDGE,"E4.30.1"),sQuery(id+"F0.wireOp",EDGE,"E4.30.2"),sQuery(id+"F0.wireOp",EDGE,"E4.31.0"),sQuery(id+"F0.wireOp",EDGE,"E4.31.1"),sQuery(id+"F0.wireOp",EDGE,"E4.31.2"),sQuery(id+"F0.wireOp",EDGE,"E4.32.0"),sQuery(id+"F0.wireOp",EDGE,"E4.32.1"),sQuery(id+"F0.wireOp",EDGE,"E4.32.2"),sQuery(id+"F0.wireOp",EDGE,"E4.33.0"),sQuery(id+"F0.wireOp",EDGE,"E4.33.1"),sQuery(id+"F0.wireOp",EDGE,"E4.33.2"),sQuery(id+"F0.wireOp",EDGE,"E4.34.0"),sQuery(id+"F0.wireOp",EDGE,"E4.34.1"),sQuery(id+"F0.wireOp",EDGE,"E4.34.2"),sQuery(id+"F0.wireOp",EDGE,"E4.35.0"),sQuery(id+"F0.wireOp",EDGE,"E4.35.1"),sQuery(id+"F0.wireOp",EDGE,"E4.35.2"),sQuery(id+"F0.wireOp",EDGE,"E4.36.0"),sQuery(id+"F0.wireOp",EDGE,"E4.36.1"),sQuery(id+"F0.wireOp",EDGE,"E4.36.2"),sQuery(id+"F0.wireOp",EDGE,"E4.37.0"),sQuery(id+"F0.wireOp",EDGE,"E4.37.1"),sQuery(id+"F0.wireOp",EDGE,"E4.37.2"),sQuery(id+"F0.wireOp",EDGE,"E4.38.0"),sQuery(id+"F0.wireOp",EDGE,"E4.38.1"),sQuery(id+"F0.wireOp",EDGE,"E4.38.2"),sQuery(id+"F0.wireOp",EDGE,"E4.39.0"),sQuery(id+"F0.wireOp",EDGE,"E4.39.1"),sQuery(id+"F0.wireOp",EDGE,"E4.39.2")])],"isStart":false});
            var sketch = newSketch(context, id + "F3", { "sketchPlane" : qUnion([Q0])});
            skCircle(sketch, "E6", {"center": v(0, 0) * mm, "radius": 34 * mm});
            skSolve(sketch);
        }
        {
            var Q0;
            Q0=makeQuery(id+"F3.imprint","IMPRINT",FACE,{"disambiguationData":[TD([[makeQuery(id+"F3.imprint","IMPRINT",EDGE,{"derivedFrom":makeQuery(id+"F1.opExtrude","CAP_EDGE",EDGE,{"disambiguationData":[OSD([sQuery(id+"F0.wireOp",EDGE,"E1")])],"isStart":false})}),1.0]])]});
            var Q1;
            Q1=makeQuery(id+"F3.imprint","IMPRINT",FACE,{"disambiguationData":[TD([[makeQuery(id+"F3.imprint","IMPRINT",EDGE,{"derivedFrom":sQuery(id+"F3.wireOp",EDGE,"E6")}),1.0]])]});
            extrude(context, id + "F4", {"entities" : qUnion([Q0, Q1]), "operationType" : NewBodyOperationType.ADD, "depth" : 2 * mm, "offsetDistance" : 25 * mm});
        }
        {
            var Q0;
            Q0=makeQuery(id+"F2.imprint","IMPRINT",FACE,{"disambiguationData":[TD([[makeQuery(id+"F2.imprint","IMPRINT",EDGE,{"derivedFrom":sQuery(id+"F2.wireOp",EDGE,"E5")}),1.0]])]});
            var Q1;
            Q1=makeQuery(id+"F2.imprint","IMPRINT",FACE,{"disambiguationData":[TD([[makeQuery(id+"F2.imprint","IMPRINT",EDGE,{"derivedFrom":makeQuery(id+"F1.opExtrude","CAP_EDGE",EDGE,{"disambiguationData":[OSD([sQuery(id+"F0.wireOp",EDGE,"E1")])],"isStart":true})}),-1.0]])]});
            extrude(context, id + "F5", {"entities" : qUnion([Q0, Q1]), "operationType" : NewBodyOperationType.ADD, "oppositeDirection" : true, "depth" : 2 * mm, "offsetDistance" : 25 * mm});
        }
        {
            var Q0;
            Q0=makeQuery(id+"F4.opExtrude","CAP_FACE",FACE,{"disambiguationData":[OSD([sQuery(id+"F3.wireOp",EDGE,"E6")])],"isStart":false});
            var sketch = newSketch(context, id + "F6", { "sketchPlane" : qUnion([Q0])});
            skCircle(sketch, "E7", {"center": v(0, 0) * mm, "radius": 20 * mm});
            skSolve(sketch);
        }
        {
            var Q0;
            Q0=qSketchRegion(id+"F6",true);
            extrude(context, id + "F7", {"entities" : qUnion([Q0]), "operationType" : NewBodyOperationType.ADD, "depth" : 17 * mm, "offsetDistance" : 25 * mm});
        }
        {
            var Q0;
            Q0=makeQuery(id+"F5.boolean.opBoolean","MERGE",FACE,{"derivedFrom":[makeQuery(id+"F1.opExtrude","CAP_FACE",FACE,{"disambiguationData":[OSD([sQuery(id+"F0.wireOp",EDGE,"E0"),sQuery(id+"F0.wireOp",EDGE,"E1"),sQuery(id+"F0.wireOp",EDGE,"E2"),sQuery(id+"F0.wireOp",EDGE,"E3"),sQuery(id+"F0.wireOp",EDGE,"E4.1.0"),sQuery(id+"F0.wireOp",EDGE,"E4.1.1"),sQuery(id+"F0.wireOp",EDGE,"E4.1.2"),sQuery(id+"F0.wireOp",EDGE,"E4.2.0"),sQuery(id+"F0.wireOp",EDGE,"E4.2.1"),sQuery(id+"F0.wireOp",EDGE,"E4.2.2"),sQuery(id+"F0.wireOp",EDGE,"E4.3.0"),sQuery(id+"F0.wireOp",EDGE,"E4.3.1"),sQuery(id+"F0.wireOp",EDGE,"E4.3.2"),sQuery(id+"F0.wireOp",EDGE,"E4.4.0"),sQuery(id+"F0.wireOp",EDGE,"E4.4.1"),sQuery(id+"F0.wireOp",EDGE,"E4.4.2"),sQuery(id+"F0.wireOp",EDGE,"E4.5.0"),sQuery(id+"F0.wireOp",EDGE,"E4.5.1"),sQuery(id+"F0.wireOp",EDGE,"E4.5.2"),sQuery(id+"F0.wireOp",EDGE,"E4.6.0"),sQuery(id+"F0.wireOp",EDGE,"E4.6.1"),sQuery(id+"F0.wireOp",EDGE,"E4.6.2"),sQuery(id+"F0.wireOp",EDGE,"E4.7.0"),sQuery(id+"F0.wireOp",EDGE,"E4.7.1"),sQuery(id+"F0.wireOp",EDGE,"E4.7.2"),sQuery(id+"F0.wireOp",EDGE,"E4.8.0"),sQuery(id+"F0.wireOp",EDGE,"E4.8.1"),sQuery(id+"F0.wireOp",EDGE,"E4.8.2"),sQuery(id+"F0.wireOp",EDGE,"E4.9.0"),sQuery(id+"F0.wireOp",EDGE,"E4.9.1"),sQuery(id+"F0.wireOp",EDGE,"E4.9.2"),sQuery(id+"F0.wireOp",EDGE,"E4.10.0"),sQuery(id+"F0.wireOp",EDGE,"E4.10.1"),sQuery(id+"F0.wireOp",EDGE,"E4.10.2"),sQuery(id+"F0.wireOp",EDGE,"E4.11.0"),sQuery(id+"F0.wireOp",EDGE,"E4.11.1"),sQuery(id+"F0.wireOp",EDGE,"E4.11.2"),sQuery(id+"F0.wireOp",EDGE,"E4.12.0"),sQuery(id+"F0.wireOp",EDGE,"E4.12.1"),sQuery(id+"F0.wireOp",EDGE,"E4.12.2"),sQuery(id+"F0.wireOp",EDGE,"E4.13.0"),sQuery(id+"F0.wireOp",EDGE,"E4.13.1"),sQuery(id+"F0.wireOp",EDGE,"E4.13.2"),sQuery(id+"F0.wireOp",EDGE,"E4.14.0"),sQuery(id+"F0.wireOp",EDGE,"E4.14.1"),sQuery(id+"F0.wireOp",EDGE,"E4.14.2"),sQuery(id+"F0.wireOp",EDGE,"E4.15.0"),sQuery(id+"F0.wireOp",EDGE,"E4.15.1"),sQuery(id+"F0.wireOp",EDGE,"E4.15.2"),sQuery(id+"F0.wireOp",EDGE,"E4.16.0"),sQuery(id+"F0.wireOp",EDGE,"E4.16.1"),sQuery(id+"F0.wireOp",EDGE,"E4.16.2"),sQuery(id+"F0.wireOp",EDGE,"E4.17.0"),sQuery(id+"F0.wireOp",EDGE,"E4.17.1"),sQuery(id+"F0.wireOp",EDGE,"E4.17.2"),sQuery(id+"F0.wireOp",EDGE,"E4.18.0"),sQuery(id+"F0.wireOp",EDGE,"E4.18.1"),sQuery(id+"F0.wireOp",EDGE,"E4.18.2"),sQuery(id+"F0.wireOp",EDGE,"E4.19.0"),sQuery(id+"F0.wireOp",EDGE,"E4.19.1"),sQuery(id+"F0.wireOp",EDGE,"E4.19.2"),sQuery(id+"F0.wireOp",EDGE,"E4.20.0"),sQuery(id+"F0.wireOp",EDGE,"E4.20.1"),sQuery(id+"F0.wireOp",EDGE,"E4.20.2"),sQuery(id+"F0.wireOp",EDGE,"E4.21.0"),sQuery(id+"F0.wireOp",EDGE,"E4.21.1"),sQuery(id+"F0.wireOp",EDGE,"E4.21.2"),sQuery(id+"F0.wireOp",EDGE,"E4.22.0"),sQuery(id+"F0.wireOp",EDGE,"E4.22.1"),sQuery(id+"F0.wireOp",EDGE,"E4.22.2"),sQuery(id+"F0.wireOp",EDGE,"E4.23.0"),sQuery(id+"F0.wireOp",EDGE,"E4.23.1"),sQuery(id+"F0.wireOp",EDGE,"E4.23.2"),sQuery(id+"F0.wireOp",EDGE,"E4.24.0"),sQuery(id+"F0.wireOp",EDGE,"E4.24.1"),sQuery(id+"F0.wireOp",EDGE,"E4.24.2"),sQuery(id+"F0.wireOp",EDGE,"E4.25.0"),sQuery(id+"F0.wireOp",EDGE,"E4.25.1"),sQuery(id+"F0.wireOp",EDGE,"E4.25.2"),sQuery(id+"F0.wireOp",EDGE,"E4.26.0"),sQuery(id+"F0.wireOp",EDGE,"E4.26.1"),sQuery(id+"F0.wireOp",EDGE,"E4.26.2"),sQuery(id+"F0.wireOp",EDGE,"E4.27.0"),sQuery(id+"F0.wireOp",EDGE,"E4.27.1"),sQuery(id+"F0.wireOp",EDGE,"E4.27.2"),sQuery(id+"F0.wireOp",EDGE,"E4.28.0"),sQuery(id+"F0.wireOp",EDGE,"E4.28.1"),sQuery(id+"F0.wireOp",EDGE,"E4.28.2"),sQuery(id+"F0.wireOp",EDGE,"E4.29.0"),sQuery(id+"F0.wireOp",EDGE,"E4.29.1"),sQuery(id+"F0.wireOp",EDGE,"E4.29.2"),sQuery(id+"F0.wireOp",EDGE,"E4.30.0"),sQuery(id+"F0.wireOp",EDGE,"E4.30.1"),sQuery(id+"F0.wireOp",EDGE,"E4.30.2"),sQuery(id+"F0.wireOp",EDGE,"E4.31.0"),sQuery(id+"F0.wireOp",EDGE,"E4.31.1"),sQuery(id+"F0.wireOp",EDGE,"E4.31.2"),sQuery(id+"F0.wireOp",EDGE,"E4.32.0"),sQuery(id+"F0.wireOp",EDGE,"E4.32.1"),sQuery(id+"F0.wireOp",EDGE,"E4.32.2"),sQuery(id+"F0.wireOp",EDGE,"E4.33.0"),sQuery(id+"F0.wireOp",EDGE,"E4.33.1"),sQuery(id+"F0.wireOp",EDGE,"E4.33.2"),sQuery(id+"F0.wireOp",EDGE,"E4.34.0"),sQuery(id+"F0.wireOp",EDGE,"E4.34.1"),sQuery(id+"F0.wireOp",EDGE,"E4.34.2"),sQuery(id+"F0.wireOp",EDGE,"E4.35.0"),sQuery(id+"F0.wireOp",EDGE,"E4.35.1"),sQuery(id+"F0.wireOp",EDGE,"E4.35.2"),sQuery(id+"F0.wireOp",EDGE,"E4.36.0"),sQuery(id+"F0.wireOp",EDGE,"E4.36.1"),sQuery(id+"F0.wireOp",EDGE,"E4.36.2"),sQuery(id+"F0.wireOp",EDGE,"E4.37.0"),sQuery(id+"F0.wireOp",EDGE,"E4.37.1"),sQuery(id+"F0.wireOp",EDGE,"E4.37.2"),sQuery(id+"F0.wireOp",EDGE,"E4.38.0"),sQuery(id+"F0.wireOp",EDGE,"E4.38.1"),sQuery(id+"F0.wireOp",EDGE,"E4.38.2"),sQuery(id+"F0.wireOp",EDGE,"E4.39.0"),sQuery(id+"F0.wireOp",EDGE,"E4.39.1"),sQuery(id+"F0.wireOp",EDGE,"E4.39.2")])],"isStart":true}),makeQuery(id+"F5.opExtrude","CAP_FACE",FACE,{"disambiguationData":[OSD([sQuery(id+"F2.wireOp",EDGE,"E5")])],"isStart":true})]});
            var sketch = newSketch(context, id + "F8", { "sketchPlane" : qUnion([Q0])});
            skCircle(sketch, "E8.cCircle", {"center": v(0, 0) * mm, "radius": 13.76 * mm, "construction": true});
            skLineSegment(sketch, "E8.0", {"start": v(-16.87, 2.18) * mm, "end": v(-3.15, 16.72) * mm});
            skLineSegment(sketch, "E8.1", {"start": v(-3.15, 16.72) * mm, "end": v(14.93, 8.16) * mm});
            skLineSegment(sketch, "E8.2", {"start": v(14.93, 8.16) * mm, "end": v(12.37, -11.68) * mm});
            skLineSegment(sketch, "E8.3", {"start": v(12.37, -11.68) * mm, "end": v(-7.28, -15.38) * mm});
            skLineSegment(sketch, "E8.4", {"start": v(-7.28, -15.38) * mm, "end": v(-16.87, 2.18) * mm});
            skPoint(sketch, "E8.0.midPoint", {"position": v(-10, 9.45) * mm});
            skSolve(sketch);
        }
        {
            var Q0;
            Q0=makeQuery(id+"F8.imprint","IMPRINT",FACE,{"disambiguationData":[TD([[makeQuery(id+"F8.imprint","IMPRINT",EDGE,{"derivedFrom":sQuery(id+"F8.wireOp",EDGE,"E8.0")}),-1.0]])]});
            extrude(context, id + "F9", {"entities" : qUnion([Q0]), "operationType" : NewBodyOperationType.REMOVE, "oppositeDirection" : true, "depth" : 25 * mm, "offsetDistance" : 25 * mm});
        }
        {
            var Q0;
            Q0=makeQuery(id+"F7.opExtrude","CAP_FACE",FACE,{"disambiguationData":[OSD([sQuery(id+"F6.wireOp",EDGE,"E7")])],"isStart":false});
            var sketch = newSketch(context, id + "F10", { "sketchPlane" : qUnion([Q0])});
            skCircle(sketch, "E9", {"center": v(0, 0) * mm, "radius": 2.5 * mm});
            skSolve(sketch);
        }
        {
            var Q0;
            Q0=qSketchRegion(id+"F10",true);
            extrude(context, id + "F11", {"entities" : qUnion([Q0]), "operationType" : NewBodyOperationType.REMOVE, "oppositeDirection" : true, "depth" : 5 * mm, "offsetDistance" : 25 * mm});
        }
    });
